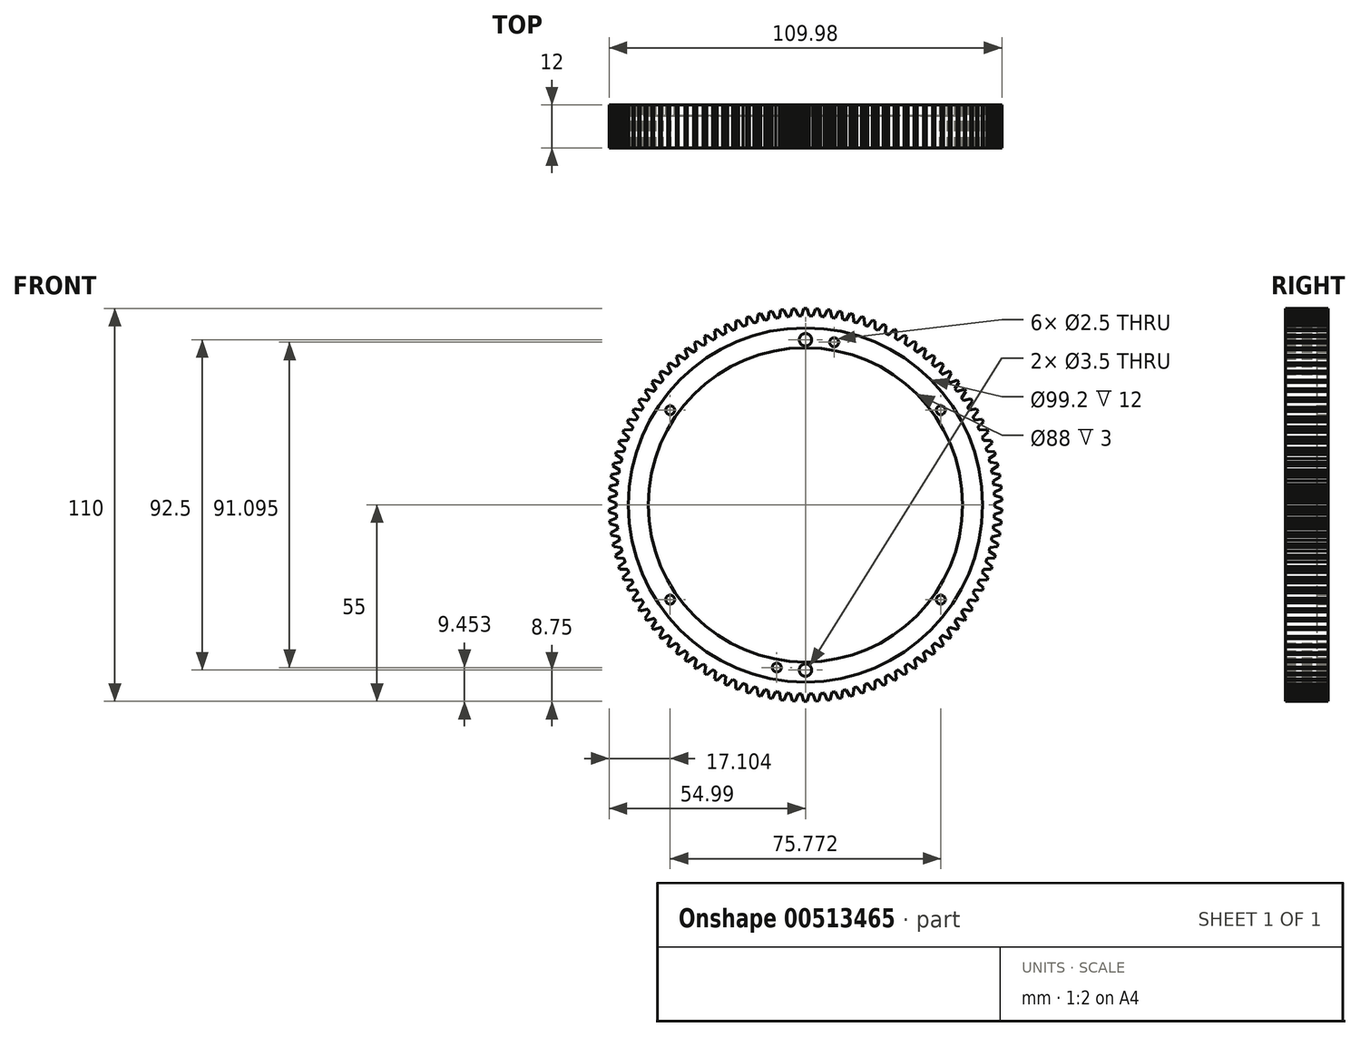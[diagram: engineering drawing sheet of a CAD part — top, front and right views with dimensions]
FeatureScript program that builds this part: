
annotation { "Feature Type Name" : "Feature", "Feature Type Description" : "" }
export const myFeature = defineFeature(function(context is Context, id is Id, definition is map)
    precondition{}
    {
        {
            var Q0;
            Q0=qCreatedBy(makeId("Front.planeOp"),FACE);
            var sketch = newSketch(context, id + "F0", { "sketchPlane" : qUnion([Q0])});
            skLineSegment(sketch, "E0", {"start": v(0, 0) * mm, "end": v(0, 53) * mm, "construction": true});
            skLineSegment(sketch, "E1", {"start": v(0, 55) * mm, "end": v(-0.4, 55) * mm});
            skLineSegment(sketch, "E2.MirrorCS", {"start": v(0, 55) * mm, "end": v(0.4, 55) * mm});
            skPoint(sketch, "E3.center", {"position": v(0, 0) * mm});
            skCircle(sketch, "E4", {"center": v(0, 0) * mm, "radius": 44 * mm});
            skCircle(sketch, "E5", {"center": v(0, 0) * mm, "radius": 46.25 * mm});
            skCircle(sketch, "E6", {"center": v(0, 0) * mm, "radius": 49.4 * mm});
            skCircle(sketch, "E7", {"center": v(0, 0) * mm, "radius": 49.6 * mm});
            skLineSegment(sketch, "E8", {"start": v(0, 0) * mm, "end": v(12.55, 71.2) * mm, "construction": true});
            skLineSegment(sketch, "E9", {"start": v(0, 0) * mm, "end": v(68.64, 48.06) * mm, "construction": true});
            skLineSegment(sketch, "E10", {"start": v(0, 0) * mm, "end": v(80.2, -56.16) * mm, "construction": true});
            skCircle(sketch, "E11", {"center": v(8.03, 45.55) * mm, "radius": 1.1 * mm});
            skCircle(sketch, "E12", {"center": v(37.89, 26.53) * mm, "radius": 1.1 * mm});
            skCircle(sketch, "E13", {"center": v(37.89, -26.53) * mm, "radius": 1.1 * mm});
            skLineSegment(sketch, "E14", {"start": v(0, 0) * mm, "end": v(0, -53) * mm, "construction": true});
            skLineSegment(sketch, "E15.MirrorCS", {"start": v(0, 0) * mm, "end": v(-80.2, -56.16) * mm, "construction": true});
            skCircle(sketch, "E16.MirrorC", {"center": v(-37.89, -26.53) * mm, "radius": 1.1 * mm});
            skLineSegment(sketch, "E17", {"start": v(0, 0) * mm, "end": v(-12.24, -69.4) * mm, "construction": true});
            skCircle(sketch, "E18", {"center": v(-8.03, -45.55) * mm, "radius": 1.1 * mm});
            skLineSegment(sketch, "E19.MirrorCS", {"start": v(0, 0) * mm, "end": v(-68.64, 48.06) * mm, "construction": true});
            skCircle(sketch, "E20.MirrorC", {"center": v(-37.89, 26.53) * mm, "radius": 1.1 * mm});
            skCircle(sketch, "E21", {"center": v(0, -46.25) * mm, "radius": 1.75 * mm});
            skCircle(sketch, "E22", {"center": v(0, 46.25) * mm, "radius": 1.75 * mm});
            skLineSegment(sketch, "E23", {"start": v(-0.4, 55) * mm, "end": v(-1.09, 52.99) * mm});
            skLineSegment(sketch, "E24", {"start": v(0.4, 55) * mm, "end": v(1.09, 52.99) * mm});
            skCircle(sketch, "E25", {"center": v(0, 0) * mm, "radius": 53 * mm});
            skLineSegment(sketch, "E26.1.0", {"start": v(-3.66, 54.88) * mm, "end": v(-4.23, 52.83) * mm});
            skLineSegment(sketch, "E26.1.1", {"start": v(-3.26, 54.9) * mm, "end": v(-3.66, 54.88) * mm});
            skLineSegment(sketch, "E26.1.2", {"start": v(-3.26, 54.9) * mm, "end": v(-2.85, 54.93) * mm});
            skLineSegment(sketch, "E26.1.3", {"start": v(-2.85, 54.93) * mm, "end": v(-2.05, 52.96) * mm});
            skLineSegment(sketch, "E26.2.0", {"start": v(-6.9, 54.57) * mm, "end": v(-7.35, 52.49) * mm});
            skLineSegment(sketch, "E26.2.1", {"start": v(-6.5, 54.61) * mm, "end": v(-6.9, 54.57) * mm});
            skLineSegment(sketch, "E26.2.2", {"start": v(-6.5, 54.61) * mm, "end": v(-6.1, 54.66) * mm});
            skLineSegment(sketch, "E26.2.3", {"start": v(-6.1, 54.66) * mm, "end": v(-5.19, 52.75) * mm});
            skLineSegment(sketch, "E26.3.0", {"start": v(-10.13, 54.06) * mm, "end": v(-10.45, 51.96) * mm});
            skLineSegment(sketch, "E26.3.1", {"start": v(-9.73, 54.13) * mm, "end": v(-10.13, 54.06) * mm});
            skLineSegment(sketch, "E26.3.2", {"start": v(-9.73, 54.13) * mm, "end": v(-9.33, 54.2) * mm});
            skLineSegment(sketch, "E26.3.3", {"start": v(-9.33, 54.2) * mm, "end": v(-8.3, 52.35) * mm});
            skLineSegment(sketch, "E26.4.0", {"start": v(-13.31, 53.37) * mm, "end": v(-13.5, 51.25) * mm});
            skLineSegment(sketch, "E26.4.1", {"start": v(-12.92, 53.46) * mm, "end": v(-13.31, 53.37) * mm});
            skLineSegment(sketch, "E26.4.2", {"start": v(-12.92, 53.46) * mm, "end": v(-12.53, 53.56) * mm});
            skLineSegment(sketch, "E26.4.3", {"start": v(-12.53, 53.56) * mm, "end": v(-11.39, 51.76) * mm});
            skLineSegment(sketch, "E26.5.0", {"start": v(-16.45, 52.48) * mm, "end": v(-16.52, 50.36) * mm});
            skLineSegment(sketch, "E26.5.1", {"start": v(-16.06, 52.6) * mm, "end": v(-16.45, 52.48) * mm});
            skLineSegment(sketch, "E26.5.2", {"start": v(-16.06, 52.6) * mm, "end": v(-15.68, 52.72) * mm});
            skLineSegment(sketch, "E26.5.3", {"start": v(-15.68, 52.72) * mm, "end": v(-14.43, 51) * mm});
            skLineSegment(sketch, "E26.6.0", {"start": v(-19.53, 51.42) * mm, "end": v(-19.47, 49.3) * mm});
            skLineSegment(sketch, "E26.6.1", {"start": v(-19.15, 51.56) * mm, "end": v(-19.53, 51.42) * mm});
            skLineSegment(sketch, "E26.6.2", {"start": v(-19.15, 51.56) * mm, "end": v(-18.77, 51.7) * mm});
            skLineSegment(sketch, "E26.6.3", {"start": v(-18.77, 51.7) * mm, "end": v(-17.43, 50.05) * mm});
            skLineSegment(sketch, "E26.7.0", {"start": v(-22.54, 50.17) * mm, "end": v(-22.36, 48.05) * mm});
            skLineSegment(sketch, "E26.7.1", {"start": v(-22.17, 50.33) * mm, "end": v(-22.54, 50.17) * mm});
            skLineSegment(sketch, "E26.7.2", {"start": v(-22.17, 50.33) * mm, "end": v(-21.8, 50.5) * mm});
            skLineSegment(sketch, "E26.7.3", {"start": v(-21.8, 50.5) * mm, "end": v(-20.36, 48.93) * mm});
            skLineSegment(sketch, "E26.8.0", {"start": v(-25.47, 48.75) * mm, "end": v(-25.17, 46.64) * mm});
            skLineSegment(sketch, "E26.8.1", {"start": v(-25.11, 48.93) * mm, "end": v(-25.47, 48.75) * mm});
            skLineSegment(sketch, "E26.8.2", {"start": v(-25.11, 48.93) * mm, "end": v(-24.75, 49.12) * mm});
            skLineSegment(sketch, "E26.8.3", {"start": v(-24.75, 49.12) * mm, "end": v(-23.23, 47.64) * mm});
            skLineSegment(sketch, "E26.9.0", {"start": v(-28.32, 47.15) * mm, "end": v(-27.88, 45.07) * mm});
            skLineSegment(sketch, "E26.9.1", {"start": v(-27.97, 47.36) * mm, "end": v(-28.32, 47.15) * mm});
            skLineSegment(sketch, "E26.9.2", {"start": v(-27.97, 47.36) * mm, "end": v(-27.62, 47.56) * mm});
            skLineSegment(sketch, "E26.9.3", {"start": v(-27.62, 47.56) * mm, "end": v(-26, 46.18) * mm});
            skLineSegment(sketch, "E26.10.0", {"start": v(-31.06, 45.4) * mm, "end": v(-30.5, 43.34) * mm});
            skLineSegment(sketch, "E26.10.1", {"start": v(-30.73, 45.62) * mm, "end": v(-31.06, 45.4) * mm});
            skLineSegment(sketch, "E26.10.2", {"start": v(-30.73, 45.62) * mm, "end": v(-30.39, 45.84) * mm});
            skLineSegment(sketch, "E26.10.3", {"start": v(-30.39, 45.84) * mm, "end": v(-28.7, 44.56) * mm});
            skLineSegment(sketch, "E26.11.0", {"start": v(-33.7, 43.47) * mm, "end": v(-33.02, 41.46) * mm});
            skLineSegment(sketch, "E26.11.1", {"start": v(-33.37, 43.72) * mm, "end": v(-33.7, 43.47) * mm});
            skLineSegment(sketch, "E26.11.2", {"start": v(-33.37, 43.72) * mm, "end": v(-33.05, 43.96) * mm});
            skLineSegment(sketch, "E26.11.3", {"start": v(-33.05, 43.96) * mm, "end": v(-31.29, 42.78) * mm});
            skLineSegment(sketch, "E26.12.0", {"start": v(-36.21, 41.4) * mm, "end": v(-35.42, 39.43) * mm});
            skLineSegment(sketch, "E26.12.1", {"start": v(-35.9, 41.66) * mm, "end": v(-36.21, 41.4) * mm});
            skLineSegment(sketch, "E26.12.2", {"start": v(-35.9, 41.66) * mm, "end": v(-35.6, 41.93) * mm});
            skLineSegment(sketch, "E26.12.3", {"start": v(-35.6, 41.93) * mm, "end": v(-33.77, 40.85) * mm});
            skLineSegment(sketch, "E26.13.0", {"start": v(-38.6, 39.18) * mm, "end": v(-37.7, 37.26) * mm});
            skLineSegment(sketch, "E26.13.1", {"start": v(-38.31, 39.46) * mm, "end": v(-38.6, 39.18) * mm});
            skLineSegment(sketch, "E26.13.2", {"start": v(-38.31, 39.46) * mm, "end": v(-38.02, 39.75) * mm});
            skLineSegment(sketch, "E26.13.3", {"start": v(-38.02, 39.75) * mm, "end": v(-36.13, 38.78) * mm});
            skLineSegment(sketch, "E26.14.0", {"start": v(-40.85, 36.83) * mm, "end": v(-39.83, 34.96) * mm});
            skLineSegment(sketch, "E26.14.1", {"start": v(-40.58, 37.12) * mm, "end": v(-40.85, 36.83) * mm});
            skLineSegment(sketch, "E26.14.2", {"start": v(-40.58, 37.12) * mm, "end": v(-40.3, 37.42) * mm});
            skLineSegment(sketch, "E26.14.3", {"start": v(-40.3, 37.42) * mm, "end": v(-38.36, 36.57) * mm});
            skLineSegment(sketch, "E26.15.0", {"start": v(-42.96, 34.34) * mm, "end": v(-41.83, 32.54) * mm});
            skLineSegment(sketch, "E26.15.1", {"start": v(-42.7, 34.65) * mm, "end": v(-42.96, 34.34) * mm});
            skLineSegment(sketch, "E26.15.2", {"start": v(-42.7, 34.65) * mm, "end": v(-42.45, 34.97) * mm});
            skLineSegment(sketch, "E26.15.3", {"start": v(-42.45, 34.97) * mm, "end": v(-40.46, 34.23) * mm});
            skLineSegment(sketch, "E27.2.16.0", {"start": v(-44.92, 31.73) * mm, "end": v(-43.69, 30) * mm});
            skLineSegment(sketch, "E27.3.16.0", {"start": v(-44.69, 32.06) * mm, "end": v(-44.92, 31.73) * mm});
            skLineSegment(sketch, "E27.6.16.0", {"start": v(-44.69, 32.06) * mm, "end": v(-44.45, 32.4) * mm});
            skLineSegment(sketch, "E27.9.16.0", {"start": v(-44.45, 32.4) * mm, "end": v(-42.42, 31.78) * mm});
            skLineSegment(sketch, "E27.2.17.0", {"start": v(-46.72, 29.02) * mm, "end": v(-45.39, 27.37) * mm});
            skLineSegment(sketch, "E27.3.17.0", {"start": v(-46.5, 29.36) * mm, "end": v(-46.72, 29.02) * mm});
            skLineSegment(sketch, "E27.6.17.0", {"start": v(-46.5, 29.36) * mm, "end": v(-46.3, 29.7) * mm});
            skLineSegment(sketch, "E27.9.17.0", {"start": v(-46.3, 29.7) * mm, "end": v(-44.23, 29.2) * mm});
            skLineSegment(sketch, "E27.2.18.0", {"start": v(-48.36, 26.2) * mm, "end": v(-46.93, 24.63) * mm});
            skLineSegment(sketch, "E27.3.18.0", {"start": v(-48.17, 26.55) * mm, "end": v(-48.36, 26.2) * mm});
            skLineSegment(sketch, "E27.6.18.0", {"start": v(-48.17, 26.55) * mm, "end": v(-47.97, 26.9) * mm});
            skLineSegment(sketch, "E27.9.18.0", {"start": v(-47.97, 26.9) * mm, "end": v(-45.88, 26.54) * mm});
            skLineSegment(sketch, "E27.2.19.0", {"start": v(-49.83, 23.29) * mm, "end": v(-48.3, 21.8) * mm});
            skLineSegment(sketch, "E27.3.19.0", {"start": v(-49.65, 23.65) * mm, "end": v(-49.83, 23.29) * mm});
            skLineSegment(sketch, "E27.6.19.0", {"start": v(-49.65, 23.65) * mm, "end": v(-49.48, 24.02) * mm});
            skLineSegment(sketch, "E27.9.19.0", {"start": v(-49.48, 24.02) * mm, "end": v(-47.37, 23.77) * mm});
            skLineSegment(sketch, "E27.2.20.0", {"start": v(-51.12, 20.3) * mm, "end": v(-49.51, 18.9) * mm});
            skLineSegment(sketch, "E27.3.20.0", {"start": v(-50.97, 20.67) * mm, "end": v(-51.12, 20.3) * mm});
            skLineSegment(sketch, "E27.6.20.0", {"start": v(-50.97, 20.67) * mm, "end": v(-50.82, 21.05) * mm});
            skLineSegment(sketch, "E27.9.20.0", {"start": v(-50.82, 21.05) * mm, "end": v(-48.7, 20.92) * mm});
            skLineSegment(sketch, "E27.2.21.0", {"start": v(-52.23, 17.23) * mm, "end": v(-50.55, 15.94) * mm});
            skLineSegment(sketch, "E27.3.21.0", {"start": v(-52.1, 17.61) * mm, "end": v(-52.23, 17.23) * mm});
            skLineSegment(sketch, "E27.6.21.0", {"start": v(-52.1, 17.61) * mm, "end": v(-51.97, 18) * mm});
            skLineSegment(sketch, "E27.9.21.0", {"start": v(-51.97, 18) * mm, "end": v(-49.85, 18) * mm});
            skLineSegment(sketch, "E27.2.22.0", {"start": v(-53.16, 14.1) * mm, "end": v(-51.4, 12.92) * mm});
            skLineSegment(sketch, "E27.3.22.0", {"start": v(-53.05, 14.5) * mm, "end": v(-53.16, 14.1) * mm});
            skLineSegment(sketch, "E27.6.22.0", {"start": v(-53.05, 14.5) * mm, "end": v(-52.95, 14.89) * mm});
            skLineSegment(sketch, "E27.9.22.0", {"start": v(-52.95, 14.89) * mm, "end": v(-50.83, 15.02) * mm});
            skLineSegment(sketch, "E27.2.23.0", {"start": v(-53.9, 10.93) * mm, "end": v(-52.08, 9.85) * mm});
            skLineSegment(sketch, "E27.3.23.0", {"start": v(-53.82, 11.33) * mm, "end": v(-53.9, 10.93) * mm});
            skLineSegment(sketch, "E27.6.23.0", {"start": v(-53.82, 11.33) * mm, "end": v(-53.74, 11.73) * mm});
            skLineSegment(sketch, "E27.9.23.0", {"start": v(-53.74, 11.73) * mm, "end": v(-51.63, 11.98) * mm});
            skLineSegment(sketch, "E27.2.24.0", {"start": v(-54.46, 7.72) * mm, "end": v(-52.57, 6.75) * mm});
            skLineSegment(sketch, "E27.3.24.0", {"start": v(-54.4, 8.12) * mm, "end": v(-54.46, 7.72) * mm});
            skLineSegment(sketch, "E27.6.24.0", {"start": v(-54.4, 8.12) * mm, "end": v(-54.34, 8.52) * mm});
            skLineSegment(sketch, "E27.9.24.0", {"start": v(-54.34, 8.52) * mm, "end": v(-52.25, 8.9) * mm});
            skLineSegment(sketch, "E27.2.25.0", {"start": v(-54.82, 4.48) * mm, "end": v(-52.88, 3.62) * mm});
            skLineSegment(sketch, "E27.3.25.0", {"start": v(-54.78, 4.88) * mm, "end": v(-54.82, 4.48) * mm});
            skLineSegment(sketch, "E27.6.25.0", {"start": v(-54.78, 4.88) * mm, "end": v(-54.75, 5.29) * mm});
            skLineSegment(sketch, "E27.9.25.0", {"start": v(-54.75, 5.29) * mm, "end": v(-52.68, 5.8) * mm});
            skLineSegment(sketch, "E27.2.26.0", {"start": v(-54.99, 1.23) * mm, "end": v(-53, 0.48) * mm});
            skLineSegment(sketch, "E27.3.26.0", {"start": v(-54.98, 1.63) * mm, "end": v(-54.99, 1.23) * mm});
            skLineSegment(sketch, "E27.6.26.0", {"start": v(-54.98, 1.63) * mm, "end": v(-54.96, 2.03) * mm});
            skLineSegment(sketch, "E27.9.26.0", {"start": v(-54.96, 2.03) * mm, "end": v(-52.93, 2.66) * mm});
            skLineSegment(sketch, "E27.2.27.0", {"start": v(-54.96, -2.03) * mm, "end": v(-52.93, -2.66) * mm});
            skLineSegment(sketch, "E27.3.27.0", {"start": v(-54.98, -1.63) * mm, "end": v(-54.96, -2.03) * mm});
            skLineSegment(sketch, "E27.6.27.0", {"start": v(-54.98, -1.63) * mm, "end": v(-54.99, -1.23) * mm});
            skLineSegment(sketch, "E27.9.27.0", {"start": v(-54.99, -1.23) * mm, "end": v(-53, -0.48) * mm});
            skLineSegment(sketch, "E27.2.28.0", {"start": v(-54.75, -5.29) * mm, "end": v(-52.68, -5.8) * mm});
            skLineSegment(sketch, "E27.3.28.0", {"start": v(-54.78, -4.88) * mm, "end": v(-54.75, -5.29) * mm});
            skLineSegment(sketch, "E27.6.28.0", {"start": v(-54.78, -4.88) * mm, "end": v(-54.82, -4.48) * mm});
            skLineSegment(sketch, "E27.9.28.0", {"start": v(-54.82, -4.48) * mm, "end": v(-52.88, -3.62) * mm});
            skLineSegment(sketch, "E27.2.29.0", {"start": v(-54.34, -8.52) * mm, "end": v(-52.25, -8.9) * mm});
            skLineSegment(sketch, "E27.3.29.0", {"start": v(-54.4, -8.12) * mm, "end": v(-54.34, -8.52) * mm});
            skLineSegment(sketch, "E27.6.29.0", {"start": v(-54.4, -8.12) * mm, "end": v(-54.46, -7.72) * mm});
            skLineSegment(sketch, "E27.9.29.0", {"start": v(-54.46, -7.72) * mm, "end": v(-52.57, -6.75) * mm});
            skLineSegment(sketch, "E27.2.30.0", {"start": v(-53.74, -11.73) * mm, "end": v(-51.63, -11.98) * mm});
            skLineSegment(sketch, "E27.3.30.0", {"start": v(-53.82, -11.33) * mm, "end": v(-53.74, -11.73) * mm});
            skLineSegment(sketch, "E27.6.30.0", {"start": v(-53.82, -11.33) * mm, "end": v(-53.9, -10.93) * mm});
            skLineSegment(sketch, "E27.9.30.0", {"start": v(-53.9, -10.93) * mm, "end": v(-52.08, -9.85) * mm});
            skLineSegment(sketch, "E27.2.31.0", {"start": v(-52.95, -14.89) * mm, "end": v(-50.83, -15.02) * mm});
            skLineSegment(sketch, "E27.3.31.0", {"start": v(-53.05, -14.5) * mm, "end": v(-52.95, -14.89) * mm});
            skLineSegment(sketch, "E27.6.31.0", {"start": v(-53.05, -14.5) * mm, "end": v(-53.16, -14.1) * mm});
            skLineSegment(sketch, "E27.9.31.0", {"start": v(-53.16, -14.1) * mm, "end": v(-51.4, -12.92) * mm});
            skLineSegment(sketch, "E27.2.32.0", {"start": v(-51.97, -18) * mm, "end": v(-49.85, -18) * mm});
            skLineSegment(sketch, "E27.3.32.0", {"start": v(-52.1, -17.61) * mm, "end": v(-51.97, -18) * mm});
            skLineSegment(sketch, "E27.6.32.0", {"start": v(-52.1, -17.61) * mm, "end": v(-52.23, -17.23) * mm});
            skLineSegment(sketch, "E27.9.32.0", {"start": v(-52.23, -17.23) * mm, "end": v(-50.55, -15.94) * mm});
            skLineSegment(sketch, "E27.2.33.0", {"start": v(-50.82, -21.05) * mm, "end": v(-48.7, -20.92) * mm});
            skLineSegment(sketch, "E27.3.33.0", {"start": v(-50.97, -20.67) * mm, "end": v(-50.82, -21.05) * mm});
            skLineSegment(sketch, "E27.6.33.0", {"start": v(-50.97, -20.67) * mm, "end": v(-51.12, -20.3) * mm});
            skLineSegment(sketch, "E27.9.33.0", {"start": v(-51.12, -20.3) * mm, "end": v(-49.51, -18.9) * mm});
            skLineSegment(sketch, "E27.2.34.0", {"start": v(-49.48, -24.02) * mm, "end": v(-47.37, -23.77) * mm});
            skLineSegment(sketch, "E27.3.34.0", {"start": v(-49.65, -23.65) * mm, "end": v(-49.48, -24.02) * mm});
            skLineSegment(sketch, "E27.6.34.0", {"start": v(-49.65, -23.65) * mm, "end": v(-49.83, -23.29) * mm});
            skLineSegment(sketch, "E27.9.34.0", {"start": v(-49.83, -23.29) * mm, "end": v(-48.3, -21.8) * mm});
            skLineSegment(sketch, "E27.2.35.0", {"start": v(-47.97, -26.9) * mm, "end": v(-45.88, -26.54) * mm});
            skLineSegment(sketch, "E27.3.35.0", {"start": v(-48.17, -26.55) * mm, "end": v(-47.97, -26.9) * mm});
            skLineSegment(sketch, "E27.6.35.0", {"start": v(-48.17, -26.55) * mm, "end": v(-48.36, -26.2) * mm});
            skLineSegment(sketch, "E27.9.35.0", {"start": v(-48.36, -26.2) * mm, "end": v(-46.93, -24.63) * mm});
            skLineSegment(sketch, "E27.2.36.0", {"start": v(-46.3, -29.7) * mm, "end": v(-44.23, -29.2) * mm});
            skLineSegment(sketch, "E27.3.36.0", {"start": v(-46.5, -29.36) * mm, "end": v(-46.3, -29.7) * mm});
            skLineSegment(sketch, "E27.6.36.0", {"start": v(-46.5, -29.36) * mm, "end": v(-46.72, -29.02) * mm});
            skLineSegment(sketch, "E27.9.36.0", {"start": v(-46.72, -29.02) * mm, "end": v(-45.39, -27.37) * mm});
            skLineSegment(sketch, "E27.2.37.0", {"start": v(-44.45, -32.4) * mm, "end": v(-42.42, -31.78) * mm});
            skLineSegment(sketch, "E27.3.37.0", {"start": v(-44.69, -32.06) * mm, "end": v(-44.45, -32.4) * mm});
            skLineSegment(sketch, "E27.6.37.0", {"start": v(-44.69, -32.06) * mm, "end": v(-44.92, -31.73) * mm});
            skLineSegment(sketch, "E27.9.37.0", {"start": v(-44.92, -31.73) * mm, "end": v(-43.69, -30) * mm});
            skLineSegment(sketch, "E27.2.38.0", {"start": v(-42.45, -34.97) * mm, "end": v(-40.46, -34.23) * mm});
            skLineSegment(sketch, "E27.3.38.0", {"start": v(-42.7, -34.65) * mm, "end": v(-42.45, -34.97) * mm});
            skLineSegment(sketch, "E27.6.38.0", {"start": v(-42.7, -34.65) * mm, "end": v(-42.96, -34.34) * mm});
            skLineSegment(sketch, "E27.9.38.0", {"start": v(-42.96, -34.34) * mm, "end": v(-41.83, -32.54) * mm});
            skLineSegment(sketch, "E27.2.39.0", {"start": v(-40.3, -37.42) * mm, "end": v(-38.36, -36.57) * mm});
            skLineSegment(sketch, "E27.3.39.0", {"start": v(-40.58, -37.12) * mm, "end": v(-40.3, -37.42) * mm});
            skLineSegment(sketch, "E27.6.39.0", {"start": v(-40.58, -37.12) * mm, "end": v(-40.85, -36.83) * mm});
            skLineSegment(sketch, "E27.9.39.0", {"start": v(-40.85, -36.83) * mm, "end": v(-39.83, -34.96) * mm});
            skLineSegment(sketch, "E27.2.40.0", {"start": v(-38.02, -39.75) * mm, "end": v(-36.13, -38.78) * mm});
            skLineSegment(sketch, "E27.3.40.0", {"start": v(-38.31, -39.46) * mm, "end": v(-38.02, -39.75) * mm});
            skLineSegment(sketch, "E27.6.40.0", {"start": v(-38.31, -39.46) * mm, "end": v(-38.6, -39.18) * mm});
            skLineSegment(sketch, "E27.9.40.0", {"start": v(-38.6, -39.18) * mm, "end": v(-37.7, -37.26) * mm});
            skLineSegment(sketch, "E27.2.41.0", {"start": v(-35.6, -41.93) * mm, "end": v(-33.77, -40.85) * mm});
            skLineSegment(sketch, "E27.3.41.0", {"start": v(-35.9, -41.66) * mm, "end": v(-35.6, -41.93) * mm});
            skLineSegment(sketch, "E27.6.41.0", {"start": v(-35.9, -41.66) * mm, "end": v(-36.21, -41.4) * mm});
            skLineSegment(sketch, "E27.9.41.0", {"start": v(-36.21, -41.4) * mm, "end": v(-35.42, -39.43) * mm});
            skLineSegment(sketch, "E27.2.42.0", {"start": v(-33.05, -43.96) * mm, "end": v(-31.29, -42.78) * mm});
            skLineSegment(sketch, "E27.3.42.0", {"start": v(-33.37, -43.72) * mm, "end": v(-33.05, -43.96) * mm});
            skLineSegment(sketch, "E27.6.42.0", {"start": v(-33.37, -43.72) * mm, "end": v(-33.7, -43.47) * mm});
            skLineSegment(sketch, "E27.9.42.0", {"start": v(-33.7, -43.47) * mm, "end": v(-33.02, -41.46) * mm});
            skLineSegment(sketch, "E27.2.43.0", {"start": v(-30.39, -45.84) * mm, "end": v(-28.7, -44.56) * mm});
            skLineSegment(sketch, "E27.3.43.0", {"start": v(-30.73, -45.62) * mm, "end": v(-30.39, -45.84) * mm});
            skLineSegment(sketch, "E27.6.43.0", {"start": v(-30.73, -45.62) * mm, "end": v(-31.06, -45.4) * mm});
            skLineSegment(sketch, "E27.9.43.0", {"start": v(-31.06, -45.4) * mm, "end": v(-30.5, -43.34) * mm});
            skLineSegment(sketch, "E27.2.44.0", {"start": v(-27.62, -47.56) * mm, "end": v(-26, -46.18) * mm});
            skLineSegment(sketch, "E27.3.44.0", {"start": v(-27.97, -47.36) * mm, "end": v(-27.62, -47.56) * mm});
            skLineSegment(sketch, "E27.6.44.0", {"start": v(-27.97, -47.36) * mm, "end": v(-28.32, -47.15) * mm});
            skLineSegment(sketch, "E27.9.44.0", {"start": v(-28.32, -47.15) * mm, "end": v(-27.88, -45.07) * mm});
            skLineSegment(sketch, "E27.2.45.0", {"start": v(-24.75, -49.12) * mm, "end": v(-23.23, -47.64) * mm});
            skLineSegment(sketch, "E27.3.45.0", {"start": v(-25.11, -48.93) * mm, "end": v(-24.75, -49.12) * mm});
            skLineSegment(sketch, "E27.6.45.0", {"start": v(-25.11, -48.93) * mm, "end": v(-25.47, -48.75) * mm});
            skLineSegment(sketch, "E27.9.45.0", {"start": v(-25.47, -48.75) * mm, "end": v(-25.17, -46.64) * mm});
            skLineSegment(sketch, "E27.2.46.0", {"start": v(-21.8, -50.5) * mm, "end": v(-20.36, -48.93) * mm});
            skLineSegment(sketch, "E27.3.46.0", {"start": v(-22.17, -50.33) * mm, "end": v(-21.8, -50.5) * mm});
            skLineSegment(sketch, "E27.6.46.0", {"start": v(-22.17, -50.33) * mm, "end": v(-22.54, -50.17) * mm});
            skLineSegment(sketch, "E27.9.46.0", {"start": v(-22.54, -50.17) * mm, "end": v(-22.36, -48.05) * mm});
            skLineSegment(sketch, "E27.2.47.0", {"start": v(-18.77, -51.7) * mm, "end": v(-17.43, -50.05) * mm});
            skLineSegment(sketch, "E27.3.47.0", {"start": v(-19.15, -51.56) * mm, "end": v(-18.77, -51.7) * mm});
            skLineSegment(sketch, "E27.6.47.0", {"start": v(-19.15, -51.56) * mm, "end": v(-19.53, -51.42) * mm});
            skLineSegment(sketch, "E27.9.47.0", {"start": v(-19.53, -51.42) * mm, "end": v(-19.47, -49.3) * mm});
            skLineSegment(sketch, "E27.2.48.0", {"start": v(-15.68, -52.72) * mm, "end": v(-14.43, -51) * mm});
            skLineSegment(sketch, "E27.3.48.0", {"start": v(-16.06, -52.6) * mm, "end": v(-15.68, -52.72) * mm});
            skLineSegment(sketch, "E27.6.48.0", {"start": v(-16.06, -52.6) * mm, "end": v(-16.45, -52.48) * mm});
            skLineSegment(sketch, "E27.9.48.0", {"start": v(-16.45, -52.48) * mm, "end": v(-16.52, -50.36) * mm});
            skLineSegment(sketch, "E27.2.49.0", {"start": v(-12.53, -53.56) * mm, "end": v(-11.39, -51.76) * mm});
            skLineSegment(sketch, "E27.3.49.0", {"start": v(-12.92, -53.46) * mm, "end": v(-12.53, -53.56) * mm});
            skLineSegment(sketch, "E27.6.49.0", {"start": v(-12.92, -53.46) * mm, "end": v(-13.31, -53.37) * mm});
            skLineSegment(sketch, "E27.9.49.0", {"start": v(-13.31, -53.37) * mm, "end": v(-13.5, -51.25) * mm});
            skLineSegment(sketch, "E27.2.50.0", {"start": v(-9.33, -54.2) * mm, "end": v(-8.3, -52.35) * mm});
            skLineSegment(sketch, "E27.3.50.0", {"start": v(-9.73, -54.13) * mm, "end": v(-9.33, -54.2) * mm});
            skLineSegment(sketch, "E27.6.50.0", {"start": v(-9.73, -54.13) * mm, "end": v(-10.13, -54.06) * mm});
            skLineSegment(sketch, "E27.9.50.0", {"start": v(-10.13, -54.06) * mm, "end": v(-10.45, -51.96) * mm});
            skLineSegment(sketch, "E27.2.51.0", {"start": v(-6.1, -54.66) * mm, "end": v(-5.19, -52.75) * mm});
            skLineSegment(sketch, "E27.3.51.0", {"start": v(-6.5, -54.61) * mm, "end": v(-6.1, -54.66) * mm});
            skLineSegment(sketch, "E27.6.51.0", {"start": v(-6.5, -54.61) * mm, "end": v(-6.9, -54.57) * mm});
            skLineSegment(sketch, "E27.9.51.0", {"start": v(-6.9, -54.57) * mm, "end": v(-7.35, -52.49) * mm});
            skLineSegment(sketch, "E27.2.52.0", {"start": v(-2.85, -54.93) * mm, "end": v(-2.05, -52.96) * mm});
            skLineSegment(sketch, "E27.3.52.0", {"start": v(-3.26, -54.9) * mm, "end": v(-2.85, -54.93) * mm});
            skLineSegment(sketch, "E27.6.52.0", {"start": v(-3.26, -54.9) * mm, "end": v(-3.66, -54.88) * mm});
            skLineSegment(sketch, "E27.9.52.0", {"start": v(-3.66, -54.88) * mm, "end": v(-4.23, -52.83) * mm});
            skLineSegment(sketch, "E27.2.53.0", {"start": v(0.4, -55) * mm, "end": v(1.09, -52.99) * mm});
            skLineSegment(sketch, "E27.3.53.0", {"start": v(0, -55) * mm, "end": v(0.4, -55) * mm});
            skLineSegment(sketch, "E27.6.53.0", {"start": v(0, -55) * mm, "end": v(-0.4, -55) * mm});
            skLineSegment(sketch, "E27.9.53.0", {"start": v(-0.4, -55) * mm, "end": v(-1.09, -52.99) * mm});
            skLineSegment(sketch, "E27.2.54.0", {"start": v(3.66, -54.88) * mm, "end": v(4.23, -52.83) * mm});
            skLineSegment(sketch, "E27.3.54.0", {"start": v(3.26, -54.9) * mm, "end": v(3.66, -54.88) * mm});
            skLineSegment(sketch, "E27.6.54.0", {"start": v(3.26, -54.9) * mm, "end": v(2.85, -54.93) * mm});
            skLineSegment(sketch, "E27.9.54.0", {"start": v(2.85, -54.93) * mm, "end": v(2.05, -52.96) * mm});
            skLineSegment(sketch, "E27.2.55.0", {"start": v(6.9, -54.57) * mm, "end": v(7.35, -52.49) * mm});
            skLineSegment(sketch, "E27.3.55.0", {"start": v(6.5, -54.61) * mm, "end": v(6.9, -54.57) * mm});
            skLineSegment(sketch, "E27.6.55.0", {"start": v(6.5, -54.61) * mm, "end": v(6.1, -54.66) * mm});
            skLineSegment(sketch, "E27.9.55.0", {"start": v(6.1, -54.66) * mm, "end": v(5.19, -52.75) * mm});
            skLineSegment(sketch, "E27.2.56.0", {"start": v(10.13, -54.06) * mm, "end": v(10.45, -51.96) * mm});
            skLineSegment(sketch, "E27.3.56.0", {"start": v(9.73, -54.13) * mm, "end": v(10.13, -54.06) * mm});
            skLineSegment(sketch, "E27.6.56.0", {"start": v(9.73, -54.13) * mm, "end": v(9.33, -54.2) * mm});
            skLineSegment(sketch, "E27.9.56.0", {"start": v(9.33, -54.2) * mm, "end": v(8.3, -52.35) * mm});
            skLineSegment(sketch, "E27.2.57.0", {"start": v(13.31, -53.37) * mm, "end": v(13.5, -51.25) * mm});
            skLineSegment(sketch, "E27.3.57.0", {"start": v(12.92, -53.46) * mm, "end": v(13.31, -53.37) * mm});
            skLineSegment(sketch, "E27.6.57.0", {"start": v(12.92, -53.46) * mm, "end": v(12.53, -53.56) * mm});
            skLineSegment(sketch, "E27.9.57.0", {"start": v(12.53, -53.56) * mm, "end": v(11.39, -51.76) * mm});
            skLineSegment(sketch, "E27.2.58.0", {"start": v(16.45, -52.48) * mm, "end": v(16.52, -50.36) * mm});
            skLineSegment(sketch, "E27.3.58.0", {"start": v(16.06, -52.6) * mm, "end": v(16.45, -52.48) * mm});
            skLineSegment(sketch, "E27.6.58.0", {"start": v(16.06, -52.6) * mm, "end": v(15.68, -52.72) * mm});
            skLineSegment(sketch, "E27.9.58.0", {"start": v(15.68, -52.72) * mm, "end": v(14.43, -51) * mm});
            skLineSegment(sketch, "E27.2.59.0", {"start": v(19.53, -51.42) * mm, "end": v(19.47, -49.3) * mm});
            skLineSegment(sketch, "E27.3.59.0", {"start": v(19.15, -51.56) * mm, "end": v(19.53, -51.42) * mm});
            skLineSegment(sketch, "E27.6.59.0", {"start": v(19.15, -51.56) * mm, "end": v(18.77, -51.7) * mm});
            skLineSegment(sketch, "E27.9.59.0", {"start": v(18.77, -51.7) * mm, "end": v(17.43, -50.05) * mm});
            skLineSegment(sketch, "E27.2.60.0", {"start": v(22.54, -50.17) * mm, "end": v(22.36, -48.05) * mm});
            skLineSegment(sketch, "E27.3.60.0", {"start": v(22.17, -50.33) * mm, "end": v(22.54, -50.17) * mm});
            skLineSegment(sketch, "E27.6.60.0", {"start": v(22.17, -50.33) * mm, "end": v(21.8, -50.5) * mm});
            skLineSegment(sketch, "E27.9.60.0", {"start": v(21.8, -50.5) * mm, "end": v(20.36, -48.93) * mm});
            skLineSegment(sketch, "E27.2.61.0", {"start": v(25.47, -48.75) * mm, "end": v(25.17, -46.64) * mm});
            skLineSegment(sketch, "E27.3.61.0", {"start": v(25.11, -48.93) * mm, "end": v(25.47, -48.75) * mm});
            skLineSegment(sketch, "E27.6.61.0", {"start": v(25.11, -48.93) * mm, "end": v(24.75, -49.12) * mm});
            skLineSegment(sketch, "E27.9.61.0", {"start": v(24.75, -49.12) * mm, "end": v(23.23, -47.64) * mm});
            skLineSegment(sketch, "E27.2.62.0", {"start": v(28.32, -47.15) * mm, "end": v(27.88, -45.07) * mm});
            skLineSegment(sketch, "E27.3.62.0", {"start": v(27.97, -47.36) * mm, "end": v(28.32, -47.15) * mm});
            skLineSegment(sketch, "E27.6.62.0", {"start": v(27.97, -47.36) * mm, "end": v(27.62, -47.56) * mm});
            skLineSegment(sketch, "E27.9.62.0", {"start": v(27.62, -47.56) * mm, "end": v(26, -46.18) * mm});
            skLineSegment(sketch, "E27.2.63.0", {"start": v(31.06, -45.4) * mm, "end": v(30.5, -43.34) * mm});
            skLineSegment(sketch, "E27.3.63.0", {"start": v(30.73, -45.62) * mm, "end": v(31.06, -45.4) * mm});
            skLineSegment(sketch, "E27.6.63.0", {"start": v(30.73, -45.62) * mm, "end": v(30.39, -45.84) * mm});
            skLineSegment(sketch, "E27.9.63.0", {"start": v(30.39, -45.84) * mm, "end": v(28.7, -44.56) * mm});
            skLineSegment(sketch, "E27.2.64.0", {"start": v(33.7, -43.47) * mm, "end": v(33.02, -41.46) * mm});
            skLineSegment(sketch, "E27.3.64.0", {"start": v(33.37, -43.72) * mm, "end": v(33.7, -43.47) * mm});
            skLineSegment(sketch, "E27.6.64.0", {"start": v(33.37, -43.72) * mm, "end": v(33.05, -43.96) * mm});
            skLineSegment(sketch, "E27.9.64.0", {"start": v(33.05, -43.96) * mm, "end": v(31.29, -42.78) * mm});
            skLineSegment(sketch, "E27.2.65.0", {"start": v(36.21, -41.4) * mm, "end": v(35.42, -39.43) * mm});
            skLineSegment(sketch, "E27.3.65.0", {"start": v(35.9, -41.66) * mm, "end": v(36.21, -41.4) * mm});
            skLineSegment(sketch, "E27.6.65.0", {"start": v(35.9, -41.66) * mm, "end": v(35.6, -41.93) * mm});
            skLineSegment(sketch, "E27.9.65.0", {"start": v(35.6, -41.93) * mm, "end": v(33.77, -40.85) * mm});
            skLineSegment(sketch, "E27.2.66.0", {"start": v(38.6, -39.18) * mm, "end": v(37.7, -37.26) * mm});
            skLineSegment(sketch, "E27.3.66.0", {"start": v(38.31, -39.46) * mm, "end": v(38.6, -39.18) * mm});
            skLineSegment(sketch, "E27.6.66.0", {"start": v(38.31, -39.46) * mm, "end": v(38.02, -39.75) * mm});
            skLineSegment(sketch, "E27.9.66.0", {"start": v(38.02, -39.75) * mm, "end": v(36.13, -38.78) * mm});
            skLineSegment(sketch, "E27.2.67.0", {"start": v(40.85, -36.83) * mm, "end": v(39.83, -34.96) * mm});
            skLineSegment(sketch, "E27.3.67.0", {"start": v(40.58, -37.12) * mm, "end": v(40.85, -36.83) * mm});
            skLineSegment(sketch, "E27.6.67.0", {"start": v(40.58, -37.12) * mm, "end": v(40.3, -37.42) * mm});
            skLineSegment(sketch, "E27.9.67.0", {"start": v(40.3, -37.42) * mm, "end": v(38.36, -36.57) * mm});
            skLineSegment(sketch, "E27.2.68.0", {"start": v(42.96, -34.34) * mm, "end": v(41.83, -32.54) * mm});
            skLineSegment(sketch, "E27.3.68.0", {"start": v(42.7, -34.65) * mm, "end": v(42.96, -34.34) * mm});
            skLineSegment(sketch, "E27.6.68.0", {"start": v(42.7, -34.65) * mm, "end": v(42.45, -34.97) * mm});
            skLineSegment(sketch, "E27.9.68.0", {"start": v(42.45, -34.97) * mm, "end": v(40.46, -34.23) * mm});
            skLineSegment(sketch, "E27.2.69.0", {"start": v(44.92, -31.73) * mm, "end": v(43.69, -30) * mm});
            skLineSegment(sketch, "E27.3.69.0", {"start": v(44.69, -32.06) * mm, "end": v(44.92, -31.73) * mm});
            skLineSegment(sketch, "E27.6.69.0", {"start": v(44.69, -32.06) * mm, "end": v(44.45, -32.4) * mm});
            skLineSegment(sketch, "E27.9.69.0", {"start": v(44.45, -32.4) * mm, "end": v(42.42, -31.78) * mm});
            skLineSegment(sketch, "E27.2.70.0", {"start": v(46.72, -29.02) * mm, "end": v(45.39, -27.37) * mm});
            skLineSegment(sketch, "E27.3.70.0", {"start": v(46.5, -29.36) * mm, "end": v(46.72, -29.02) * mm});
            skLineSegment(sketch, "E27.6.70.0", {"start": v(46.5, -29.36) * mm, "end": v(46.3, -29.7) * mm});
            skLineSegment(sketch, "E27.9.70.0", {"start": v(46.3, -29.7) * mm, "end": v(44.23, -29.2) * mm});
            skLineSegment(sketch, "E27.2.71.0", {"start": v(48.36, -26.2) * mm, "end": v(46.93, -24.63) * mm});
            skLineSegment(sketch, "E27.3.71.0", {"start": v(48.17, -26.55) * mm, "end": v(48.36, -26.2) * mm});
            skLineSegment(sketch, "E27.6.71.0", {"start": v(48.17, -26.55) * mm, "end": v(47.97, -26.9) * mm});
            skLineSegment(sketch, "E27.9.71.0", {"start": v(47.97, -26.9) * mm, "end": v(45.88, -26.54) * mm});
            skLineSegment(sketch, "E27.2.72.0", {"start": v(49.83, -23.29) * mm, "end": v(48.3, -21.8) * mm});
            skLineSegment(sketch, "E27.3.72.0", {"start": v(49.65, -23.65) * mm, "end": v(49.83, -23.29) * mm});
            skLineSegment(sketch, "E27.6.72.0", {"start": v(49.65, -23.65) * mm, "end": v(49.48, -24.02) * mm});
            skLineSegment(sketch, "E27.9.72.0", {"start": v(49.48, -24.02) * mm, "end": v(47.37, -23.77) * mm});
            skLineSegment(sketch, "E27.2.73.0", {"start": v(51.12, -20.3) * mm, "end": v(49.51, -18.9) * mm});
            skLineSegment(sketch, "E27.3.73.0", {"start": v(50.97, -20.67) * mm, "end": v(51.12, -20.3) * mm});
            skLineSegment(sketch, "E27.6.73.0", {"start": v(50.97, -20.67) * mm, "end": v(50.82, -21.05) * mm});
            skLineSegment(sketch, "E27.9.73.0", {"start": v(50.82, -21.05) * mm, "end": v(48.7, -20.92) * mm});
            skLineSegment(sketch, "E27.2.74.0", {"start": v(52.23, -17.23) * mm, "end": v(50.55, -15.94) * mm});
            skLineSegment(sketch, "E27.3.74.0", {"start": v(52.1, -17.61) * mm, "end": v(52.23, -17.23) * mm});
            skLineSegment(sketch, "E27.6.74.0", {"start": v(52.1, -17.61) * mm, "end": v(51.97, -18) * mm});
            skLineSegment(sketch, "E27.9.74.0", {"start": v(51.97, -18) * mm, "end": v(49.85, -18) * mm});
            skLineSegment(sketch, "E27.2.75.0", {"start": v(53.16, -14.1) * mm, "end": v(51.4, -12.92) * mm});
            skLineSegment(sketch, "E27.3.75.0", {"start": v(53.05, -14.5) * mm, "end": v(53.16, -14.1) * mm});
            skLineSegment(sketch, "E27.6.75.0", {"start": v(53.05, -14.5) * mm, "end": v(52.95, -14.89) * mm});
            skLineSegment(sketch, "E27.9.75.0", {"start": v(52.95, -14.89) * mm, "end": v(50.83, -15.02) * mm});
            skLineSegment(sketch, "E27.2.76.0", {"start": v(53.9, -10.93) * mm, "end": v(52.08, -9.85) * mm});
            skLineSegment(sketch, "E27.3.76.0", {"start": v(53.82, -11.33) * mm, "end": v(53.9, -10.93) * mm});
            skLineSegment(sketch, "E27.6.76.0", {"start": v(53.82, -11.33) * mm, "end": v(53.74, -11.73) * mm});
            skLineSegment(sketch, "E27.9.76.0", {"start": v(53.74, -11.73) * mm, "end": v(51.63, -11.98) * mm});
            skLineSegment(sketch, "E27.2.77.0", {"start": v(54.46, -7.72) * mm, "end": v(52.57, -6.75) * mm});
            skLineSegment(sketch, "E27.3.77.0", {"start": v(54.4, -8.12) * mm, "end": v(54.46, -7.72) * mm});
            skLineSegment(sketch, "E27.6.77.0", {"start": v(54.4, -8.12) * mm, "end": v(54.34, -8.52) * mm});
            skLineSegment(sketch, "E27.9.77.0", {"start": v(54.34, -8.52) * mm, "end": v(52.25, -8.9) * mm});
            skLineSegment(sketch, "E27.2.78.0", {"start": v(54.82, -4.48) * mm, "end": v(52.88, -3.62) * mm});
            skLineSegment(sketch, "E27.3.78.0", {"start": v(54.78, -4.88) * mm, "end": v(54.82, -4.48) * mm});
            skLineSegment(sketch, "E27.6.78.0", {"start": v(54.78, -4.88) * mm, "end": v(54.75, -5.29) * mm});
            skLineSegment(sketch, "E27.9.78.0", {"start": v(54.75, -5.29) * mm, "end": v(52.68, -5.8) * mm});
            skLineSegment(sketch, "E27.2.79.0", {"start": v(54.99, -1.23) * mm, "end": v(53, -0.48) * mm});
            skLineSegment(sketch, "E27.3.79.0", {"start": v(54.98, -1.63) * mm, "end": v(54.99, -1.23) * mm});
            skLineSegment(sketch, "E27.6.79.0", {"start": v(54.98, -1.63) * mm, "end": v(54.96, -2.03) * mm});
            skLineSegment(sketch, "E27.9.79.0", {"start": v(54.96, -2.03) * mm, "end": v(52.93, -2.66) * mm});
            skLineSegment(sketch, "E27.2.80.0", {"start": v(54.96, 2.03) * mm, "end": v(52.93, 2.66) * mm});
            skLineSegment(sketch, "E27.3.80.0", {"start": v(54.98, 1.63) * mm, "end": v(54.96, 2.03) * mm});
            skLineSegment(sketch, "E27.6.80.0", {"start": v(54.98, 1.63) * mm, "end": v(54.99, 1.23) * mm});
            skLineSegment(sketch, "E27.9.80.0", {"start": v(54.99, 1.23) * mm, "end": v(53, 0.48) * mm});
            skLineSegment(sketch, "E27.2.81.0", {"start": v(54.75, 5.29) * mm, "end": v(52.68, 5.8) * mm});
            skLineSegment(sketch, "E27.3.81.0", {"start": v(54.78, 4.88) * mm, "end": v(54.75, 5.29) * mm});
            skLineSegment(sketch, "E27.6.81.0", {"start": v(54.78, 4.88) * mm, "end": v(54.82, 4.48) * mm});
            skLineSegment(sketch, "E27.9.81.0", {"start": v(54.82, 4.48) * mm, "end": v(52.88, 3.62) * mm});
            skLineSegment(sketch, "E27.2.82.0", {"start": v(54.34, 8.52) * mm, "end": v(52.25, 8.9) * mm});
            skLineSegment(sketch, "E27.3.82.0", {"start": v(54.4, 8.12) * mm, "end": v(54.34, 8.52) * mm});
            skLineSegment(sketch, "E27.6.82.0", {"start": v(54.4, 8.12) * mm, "end": v(54.46, 7.72) * mm});
            skLineSegment(sketch, "E27.9.82.0", {"start": v(54.46, 7.72) * mm, "end": v(52.57, 6.75) * mm});
            skLineSegment(sketch, "E27.2.83.0", {"start": v(53.74, 11.73) * mm, "end": v(51.63, 11.98) * mm});
            skLineSegment(sketch, "E27.3.83.0", {"start": v(53.82, 11.33) * mm, "end": v(53.74, 11.73) * mm});
            skLineSegment(sketch, "E27.6.83.0", {"start": v(53.82, 11.33) * mm, "end": v(53.9, 10.93) * mm});
            skLineSegment(sketch, "E27.9.83.0", {"start": v(53.9, 10.93) * mm, "end": v(52.08, 9.85) * mm});
            skLineSegment(sketch, "E27.2.84.0", {"start": v(52.95, 14.89) * mm, "end": v(50.83, 15.02) * mm});
            skLineSegment(sketch, "E27.3.84.0", {"start": v(53.05, 14.5) * mm, "end": v(52.95, 14.89) * mm});
            skLineSegment(sketch, "E27.6.84.0", {"start": v(53.05, 14.5) * mm, "end": v(53.16, 14.1) * mm});
            skLineSegment(sketch, "E27.9.84.0", {"start": v(53.16, 14.1) * mm, "end": v(51.4, 12.92) * mm});
            skLineSegment(sketch, "E27.2.85.0", {"start": v(51.97, 18) * mm, "end": v(49.85, 18) * mm});
            skLineSegment(sketch, "E27.3.85.0", {"start": v(52.1, 17.61) * mm, "end": v(51.97, 18) * mm});
            skLineSegment(sketch, "E27.6.85.0", {"start": v(52.1, 17.61) * mm, "end": v(52.23, 17.23) * mm});
            skLineSegment(sketch, "E27.9.85.0", {"start": v(52.23, 17.23) * mm, "end": v(50.55, 15.94) * mm});
            skLineSegment(sketch, "E27.2.86.0", {"start": v(50.82, 21.05) * mm, "end": v(48.7, 20.92) * mm});
            skLineSegment(sketch, "E27.3.86.0", {"start": v(50.97, 20.67) * mm, "end": v(50.82, 21.05) * mm});
            skLineSegment(sketch, "E27.6.86.0", {"start": v(50.97, 20.67) * mm, "end": v(51.12, 20.3) * mm});
            skLineSegment(sketch, "E27.9.86.0", {"start": v(51.12, 20.3) * mm, "end": v(49.51, 18.9) * mm});
            skLineSegment(sketch, "E27.2.87.0", {"start": v(49.48, 24.02) * mm, "end": v(47.37, 23.77) * mm});
            skLineSegment(sketch, "E27.3.87.0", {"start": v(49.65, 23.65) * mm, "end": v(49.48, 24.02) * mm});
            skLineSegment(sketch, "E27.6.87.0", {"start": v(49.65, 23.65) * mm, "end": v(49.83, 23.29) * mm});
            skLineSegment(sketch, "E27.9.87.0", {"start": v(49.83, 23.29) * mm, "end": v(48.3, 21.8) * mm});
            skLineSegment(sketch, "E27.2.88.0", {"start": v(47.97, 26.9) * mm, "end": v(45.88, 26.54) * mm});
            skLineSegment(sketch, "E27.3.88.0", {"start": v(48.17, 26.55) * mm, "end": v(47.97, 26.9) * mm});
            skLineSegment(sketch, "E27.6.88.0", {"start": v(48.17, 26.55) * mm, "end": v(48.36, 26.2) * mm});
            skLineSegment(sketch, "E27.9.88.0", {"start": v(48.36, 26.2) * mm, "end": v(46.93, 24.63) * mm});
            skLineSegment(sketch, "E27.2.89.0", {"start": v(46.3, 29.7) * mm, "end": v(44.23, 29.2) * mm});
            skLineSegment(sketch, "E27.3.89.0", {"start": v(46.5, 29.36) * mm, "end": v(46.3, 29.7) * mm});
            skLineSegment(sketch, "E27.6.89.0", {"start": v(46.5, 29.36) * mm, "end": v(46.72, 29.02) * mm});
            skLineSegment(sketch, "E27.9.89.0", {"start": v(46.72, 29.02) * mm, "end": v(45.39, 27.37) * mm});
            skLineSegment(sketch, "E27.2.90.0", {"start": v(44.45, 32.4) * mm, "end": v(42.42, 31.78) * mm});
            skLineSegment(sketch, "E27.3.90.0", {"start": v(44.69, 32.06) * mm, "end": v(44.45, 32.4) * mm});
            skLineSegment(sketch, "E27.6.90.0", {"start": v(44.69, 32.06) * mm, "end": v(44.92, 31.73) * mm});
            skLineSegment(sketch, "E27.9.90.0", {"start": v(44.92, 31.73) * mm, "end": v(43.69, 30) * mm});
            skLineSegment(sketch, "E27.2.91.0", {"start": v(42.45, 34.97) * mm, "end": v(40.46, 34.23) * mm});
            skLineSegment(sketch, "E27.3.91.0", {"start": v(42.7, 34.65) * mm, "end": v(42.45, 34.97) * mm});
            skLineSegment(sketch, "E27.6.91.0", {"start": v(42.7, 34.65) * mm, "end": v(42.96, 34.34) * mm});
            skLineSegment(sketch, "E27.9.91.0", {"start": v(42.96, 34.34) * mm, "end": v(41.83, 32.54) * mm});
            skLineSegment(sketch, "E27.2.92.0", {"start": v(40.3, 37.42) * mm, "end": v(38.36, 36.57) * mm});
            skLineSegment(sketch, "E27.3.92.0", {"start": v(40.58, 37.12) * mm, "end": v(40.3, 37.42) * mm});
            skLineSegment(sketch, "E27.6.92.0", {"start": v(40.58, 37.12) * mm, "end": v(40.85, 36.83) * mm});
            skLineSegment(sketch, "E27.9.92.0", {"start": v(40.85, 36.83) * mm, "end": v(39.83, 34.96) * mm});
            skLineSegment(sketch, "E27.2.93.0", {"start": v(38.02, 39.75) * mm, "end": v(36.13, 38.78) * mm});
            skLineSegment(sketch, "E27.3.93.0", {"start": v(38.31, 39.46) * mm, "end": v(38.02, 39.75) * mm});
            skLineSegment(sketch, "E27.6.93.0", {"start": v(38.31, 39.46) * mm, "end": v(38.6, 39.18) * mm});
            skLineSegment(sketch, "E27.9.93.0", {"start": v(38.6, 39.18) * mm, "end": v(37.7, 37.26) * mm});
            skLineSegment(sketch, "E27.2.94.0", {"start": v(35.6, 41.93) * mm, "end": v(33.77, 40.85) * mm});
            skLineSegment(sketch, "E27.3.94.0", {"start": v(35.9, 41.66) * mm, "end": v(35.6, 41.93) * mm});
            skLineSegment(sketch, "E27.6.94.0", {"start": v(35.9, 41.66) * mm, "end": v(36.21, 41.4) * mm});
            skLineSegment(sketch, "E27.9.94.0", {"start": v(36.21, 41.4) * mm, "end": v(35.42, 39.43) * mm});
            skLineSegment(sketch, "E27.2.95.0", {"start": v(33.05, 43.96) * mm, "end": v(31.29, 42.78) * mm});
            skLineSegment(sketch, "E27.3.95.0", {"start": v(33.37, 43.72) * mm, "end": v(33.05, 43.96) * mm});
            skLineSegment(sketch, "E27.6.95.0", {"start": v(33.37, 43.72) * mm, "end": v(33.7, 43.47) * mm});
            skLineSegment(sketch, "E27.9.95.0", {"start": v(33.7, 43.47) * mm, "end": v(33.02, 41.46) * mm});
            skLineSegment(sketch, "E27.2.96.0", {"start": v(30.39, 45.84) * mm, "end": v(28.7, 44.56) * mm});
            skLineSegment(sketch, "E27.3.96.0", {"start": v(30.73, 45.62) * mm, "end": v(30.39, 45.84) * mm});
            skLineSegment(sketch, "E27.6.96.0", {"start": v(30.73, 45.62) * mm, "end": v(31.06, 45.4) * mm});
            skLineSegment(sketch, "E27.9.96.0", {"start": v(31.06, 45.4) * mm, "end": v(30.5, 43.34) * mm});
            skLineSegment(sketch, "E27.2.97.0", {"start": v(27.62, 47.56) * mm, "end": v(26, 46.18) * mm});
            skLineSegment(sketch, "E27.3.97.0", {"start": v(27.97, 47.36) * mm, "end": v(27.62, 47.56) * mm});
            skLineSegment(sketch, "E27.6.97.0", {"start": v(27.97, 47.36) * mm, "end": v(28.32, 47.15) * mm});
            skLineSegment(sketch, "E27.9.97.0", {"start": v(28.32, 47.15) * mm, "end": v(27.88, 45.07) * mm});
            skLineSegment(sketch, "E27.2.98.0", {"start": v(24.75, 49.12) * mm, "end": v(23.23, 47.64) * mm});
            skLineSegment(sketch, "E27.3.98.0", {"start": v(25.11, 48.93) * mm, "end": v(24.75, 49.12) * mm});
            skLineSegment(sketch, "E27.6.98.0", {"start": v(25.11, 48.93) * mm, "end": v(25.47, 48.75) * mm});
            skLineSegment(sketch, "E27.9.98.0", {"start": v(25.47, 48.75) * mm, "end": v(25.17, 46.64) * mm});
            skLineSegment(sketch, "E27.2.99.0", {"start": v(21.8, 50.5) * mm, "end": v(20.36, 48.93) * mm});
            skLineSegment(sketch, "E27.3.99.0", {"start": v(22.17, 50.33) * mm, "end": v(21.8, 50.5) * mm});
            skLineSegment(sketch, "E27.6.99.0", {"start": v(22.17, 50.33) * mm, "end": v(22.54, 50.17) * mm});
            skLineSegment(sketch, "E27.9.99.0", {"start": v(22.54, 50.17) * mm, "end": v(22.36, 48.05) * mm});
            skLineSegment(sketch, "E27.2.100.0", {"start": v(18.77, 51.7) * mm, "end": v(17.43, 50.05) * mm});
            skLineSegment(sketch, "E27.3.100.0", {"start": v(19.15, 51.56) * mm, "end": v(18.77, 51.7) * mm});
            skLineSegment(sketch, "E27.6.100.0", {"start": v(19.15, 51.56) * mm, "end": v(19.53, 51.42) * mm});
            skLineSegment(sketch, "E27.9.100.0", {"start": v(19.53, 51.42) * mm, "end": v(19.47, 49.3) * mm});
            skLineSegment(sketch, "E27.2.101.0", {"start": v(15.68, 52.72) * mm, "end": v(14.43, 51) * mm});
            skLineSegment(sketch, "E27.3.101.0", {"start": v(16.06, 52.6) * mm, "end": v(15.68, 52.72) * mm});
            skLineSegment(sketch, "E27.6.101.0", {"start": v(16.06, 52.6) * mm, "end": v(16.45, 52.48) * mm});
            skLineSegment(sketch, "E27.9.101.0", {"start": v(16.45, 52.48) * mm, "end": v(16.52, 50.36) * mm});
            skLineSegment(sketch, "E27.2.102.0", {"start": v(12.53, 53.56) * mm, "end": v(11.39, 51.76) * mm});
            skLineSegment(sketch, "E27.3.102.0", {"start": v(12.92, 53.46) * mm, "end": v(12.53, 53.56) * mm});
            skLineSegment(sketch, "E27.6.102.0", {"start": v(12.92, 53.46) * mm, "end": v(13.31, 53.37) * mm});
            skLineSegment(sketch, "E27.9.102.0", {"start": v(13.31, 53.37) * mm, "end": v(13.5, 51.25) * mm});
            skLineSegment(sketch, "E27.2.103.0", {"start": v(9.33, 54.2) * mm, "end": v(8.3, 52.35) * mm});
            skLineSegment(sketch, "E27.3.103.0", {"start": v(9.73, 54.13) * mm, "end": v(9.33, 54.2) * mm});
            skLineSegment(sketch, "E27.6.103.0", {"start": v(9.73, 54.13) * mm, "end": v(10.13, 54.06) * mm});
            skLineSegment(sketch, "E27.9.103.0", {"start": v(10.13, 54.06) * mm, "end": v(10.45, 51.96) * mm});
            skLineSegment(sketch, "E27.2.104.0", {"start": v(6.1, 54.66) * mm, "end": v(5.19, 52.75) * mm});
            skLineSegment(sketch, "E27.3.104.0", {"start": v(6.5, 54.61) * mm, "end": v(6.1, 54.66) * mm});
            skLineSegment(sketch, "E27.6.104.0", {"start": v(6.5, 54.61) * mm, "end": v(6.9, 54.57) * mm});
            skLineSegment(sketch, "E27.9.104.0", {"start": v(6.9, 54.57) * mm, "end": v(7.35, 52.49) * mm});
            skLineSegment(sketch, "E27.2.105.0", {"start": v(2.85, 54.93) * mm, "end": v(2.05, 52.96) * mm});
            skLineSegment(sketch, "E27.3.105.0", {"start": v(3.26, 54.9) * mm, "end": v(2.85, 54.93) * mm});
            skLineSegment(sketch, "E27.6.105.0", {"start": v(3.26, 54.9) * mm, "end": v(3.66, 54.88) * mm});
            skLineSegment(sketch, "E27.9.105.0", {"start": v(3.66, 54.88) * mm, "end": v(4.23, 52.83) * mm});
            skSolve(sketch);
        }
        {
            var Q0;
            Q0=makeQuery(id+"F0.imprint","IMPRINT",FACE,{"disambiguationData":[TD([[makeQuery(id+"F0.imprint","IMPRINT",EDGE,{"derivedFrom":sQuery(id+"F0.wireOp",EDGE,"E4")}),-1.0]])]});
            var Q1;
            Q1=makeQuery(id+"F0.imprint","IMPRINT",FACE,{"disambiguationData":[TD([[makeQuery(id+"F0.imprint","IMPRINT",EDGE,{"derivedFrom":sQuery(id+"F0.wireOp",EDGE,"E6")}),1.0]])]});
            var Q2;
            {var subQ0=sQuery(id+"F0.wireOp",EDGE,"E16.MirrorC");var subQ1=sQuery(id+"F0.wireOp",EDGE,"E5");var subQ2=makeQuery(id+"F0.imprint","INTERSECT",VERTEX,{"disambiguationData":[OD(0.0)],"derivedFrom":[subQ1,subQ0]});Q2=makeQuery(id+"F0.imprint","IMPRINT",FACE,{"disambiguationData":[TD([[makeQuery(id+"F0.imprint","IMPRINT",EDGE,{"disambiguationData":[TD([[subQ2,-1.0]])],"derivedFrom":subQ1}),-1.0]])]});}
            var Q3;
            {var subQ0=sQuery(id+"F0.wireOp",EDGE,"E16.MirrorC");var subQ1=sQuery(id+"F0.wireOp",EDGE,"E5");var subQ2=makeQuery(id+"F0.imprint","INTERSECT",VERTEX,{"disambiguationData":[OD(0.0)],"derivedFrom":[subQ1,subQ0]});Q3=makeQuery(id+"F0.imprint","IMPRINT",FACE,{"disambiguationData":[TD([[makeQuery(id+"F0.imprint","IMPRINT",EDGE,{"disambiguationData":[TD([[subQ2,-1.0]])],"derivedFrom":subQ1}),1.0]])]});}
            var Q4;
            {var subQ0=sQuery(id+"F0.wireOp",EDGE,"E18");var subQ1=sQuery(id+"F0.wireOp",EDGE,"E5");var subQ2=makeQuery(id+"F0.imprint","INTERSECT",VERTEX,{"disambiguationData":[OD(0.0)],"derivedFrom":[subQ1,subQ0]});Q4=makeQuery(id+"F0.imprint","IMPRINT",FACE,{"disambiguationData":[TD([[makeQuery(id+"F0.imprint","IMPRINT",EDGE,{"disambiguationData":[TD([[subQ2,-1.0]])],"derivedFrom":subQ1}),-1.0]])]});}
            var Q5;
            {var subQ0=sQuery(id+"F0.wireOp",EDGE,"E18");var subQ1=sQuery(id+"F0.wireOp",EDGE,"E5");var subQ2=makeQuery(id+"F0.imprint","INTERSECT",VERTEX,{"disambiguationData":[OD(0.0)],"derivedFrom":[subQ1,subQ0]});Q5=makeQuery(id+"F0.imprint","IMPRINT",FACE,{"disambiguationData":[TD([[makeQuery(id+"F0.imprint","IMPRINT",EDGE,{"disambiguationData":[TD([[subQ2,-1.0]])],"derivedFrom":subQ1}),1.0]])]});}
            var Q6;
            {var subQ0=sQuery(id+"F0.wireOp",EDGE,"E21");var subQ1=sQuery(id+"F0.wireOp",EDGE,"E5");var subQ2=makeQuery(id+"F0.imprint","INTERSECT",VERTEX,{"disambiguationData":[OD(0.0)],"derivedFrom":[subQ1,subQ0]});Q6=makeQuery(id+"F0.imprint","IMPRINT",FACE,{"disambiguationData":[TD([[makeQuery(id+"F0.imprint","IMPRINT",EDGE,{"disambiguationData":[TD([[subQ2,-1.0]])],"derivedFrom":subQ1}),-1.0]])]});}
            var Q7;
            {var subQ0=sQuery(id+"F0.wireOp",EDGE,"E21");var subQ1=sQuery(id+"F0.wireOp",EDGE,"E5");var subQ2=makeQuery(id+"F0.imprint","INTERSECT",VERTEX,{"disambiguationData":[OD(0.0)],"derivedFrom":[subQ1,subQ0]});Q7=makeQuery(id+"F0.imprint","IMPRINT",FACE,{"disambiguationData":[TD([[makeQuery(id+"F0.imprint","IMPRINT",EDGE,{"disambiguationData":[TD([[subQ2,-1.0]])],"derivedFrom":subQ1}),1.0]])]});}
            var Q8;
            {var subQ0=sQuery(id+"F0.wireOp",EDGE,"E13");var subQ1=sQuery(id+"F0.wireOp",EDGE,"E5");var subQ2=makeQuery(id+"F0.imprint","INTERSECT",VERTEX,{"disambiguationData":[OD(0.0)],"derivedFrom":[subQ1,subQ0]});Q8=makeQuery(id+"F0.imprint","IMPRINT",FACE,{"disambiguationData":[TD([[makeQuery(id+"F0.imprint","IMPRINT",EDGE,{"disambiguationData":[TD([[subQ2,-1.0]])],"derivedFrom":subQ1}),-1.0]])]});}
            var Q9;
            {var subQ0=sQuery(id+"F0.wireOp",EDGE,"E13");var subQ1=sQuery(id+"F0.wireOp",EDGE,"E5");var subQ2=makeQuery(id+"F0.imprint","INTERSECT",VERTEX,{"disambiguationData":[OD(0.0)],"derivedFrom":[subQ1,subQ0]});Q9=makeQuery(id+"F0.imprint","IMPRINT",FACE,{"disambiguationData":[TD([[makeQuery(id+"F0.imprint","IMPRINT",EDGE,{"disambiguationData":[TD([[subQ2,-1.0]])],"derivedFrom":subQ1}),1.0]])]});}
            var Q10;
            {var subQ0=sQuery(id+"F0.wireOp",EDGE,"E12");var subQ1=sQuery(id+"F0.wireOp",EDGE,"E5");var subQ2=makeQuery(id+"F0.imprint","INTERSECT",VERTEX,{"disambiguationData":[OD(0.0)],"derivedFrom":[subQ1,subQ0]});Q10=makeQuery(id+"F0.imprint","IMPRINT",FACE,{"disambiguationData":[TD([[makeQuery(id+"F0.imprint","IMPRINT",EDGE,{"disambiguationData":[TD([[subQ2,1.0]])],"derivedFrom":subQ1}),-1.0]])]});}
            var Q11;
            {var subQ0=sQuery(id+"F0.wireOp",EDGE,"E12");var subQ1=sQuery(id+"F0.wireOp",EDGE,"E5");var subQ2=makeQuery(id+"F0.imprint","INTERSECT",VERTEX,{"disambiguationData":[OD(0.0)],"derivedFrom":[subQ1,subQ0]});Q11=makeQuery(id+"F0.imprint","IMPRINT",FACE,{"disambiguationData":[TD([[makeQuery(id+"F0.imprint","IMPRINT",EDGE,{"disambiguationData":[TD([[subQ2,1.0]])],"derivedFrom":subQ1}),1.0]])]});}
            var Q12;
            {var subQ0=sQuery(id+"F0.wireOp",EDGE,"E22");var subQ1=sQuery(id+"F0.wireOp",EDGE,"E5");var subQ2=makeQuery(id+"F0.imprint","INTERSECT",VERTEX,{"disambiguationData":[OD(0.0)],"derivedFrom":[subQ1,subQ0]});Q12=makeQuery(id+"F0.imprint","IMPRINT",FACE,{"disambiguationData":[TD([[makeQuery(id+"F0.imprint","IMPRINT",EDGE,{"disambiguationData":[TD([[subQ2,-1.0]])],"derivedFrom":subQ1}),1.0]])]});}
            var Q13;
            {var subQ0=sQuery(id+"F0.wireOp",EDGE,"E22");var subQ1=sQuery(id+"F0.wireOp",EDGE,"E5");var subQ2=makeQuery(id+"F0.imprint","INTERSECT",VERTEX,{"disambiguationData":[OD(0.0)],"derivedFrom":[subQ1,subQ0]});Q13=makeQuery(id+"F0.imprint","IMPRINT",FACE,{"disambiguationData":[TD([[makeQuery(id+"F0.imprint","IMPRINT",EDGE,{"disambiguationData":[TD([[subQ2,-1.0]])],"derivedFrom":subQ1}),-1.0]])]});}
            var Q14;
            {var subQ0=sQuery(id+"F0.wireOp",EDGE,"E11");var subQ1=sQuery(id+"F0.wireOp",EDGE,"E5");var subQ2=makeQuery(id+"F0.imprint","INTERSECT",VERTEX,{"disambiguationData":[OD(0.0)],"derivedFrom":[subQ1,subQ0]});Q14=makeQuery(id+"F0.imprint","IMPRINT",FACE,{"disambiguationData":[TD([[makeQuery(id+"F0.imprint","IMPRINT",EDGE,{"disambiguationData":[TD([[subQ2,-1.0]])],"derivedFrom":subQ1}),1.0]])]});}
            var Q15;
            {var subQ0=sQuery(id+"F0.wireOp",EDGE,"E11");var subQ1=sQuery(id+"F0.wireOp",EDGE,"E5");var subQ2=makeQuery(id+"F0.imprint","INTERSECT",VERTEX,{"disambiguationData":[OD(0.0)],"derivedFrom":[subQ1,subQ0]});Q15=makeQuery(id+"F0.imprint","IMPRINT",FACE,{"disambiguationData":[TD([[makeQuery(id+"F0.imprint","IMPRINT",EDGE,{"disambiguationData":[TD([[subQ2,-1.0]])],"derivedFrom":subQ1}),-1.0]])]});}
            var Q16;
            {var subQ0=sQuery(id+"F0.wireOp",EDGE,"E20.MirrorC");var subQ1=sQuery(id+"F0.wireOp",EDGE,"E5");var subQ2=makeQuery(id+"F0.imprint","INTERSECT",VERTEX,{"disambiguationData":[OD(0.0)],"derivedFrom":[subQ1,subQ0]});Q16=makeQuery(id+"F0.imprint","IMPRINT",FACE,{"disambiguationData":[TD([[makeQuery(id+"F0.imprint","IMPRINT",EDGE,{"disambiguationData":[TD([[subQ2,-1.0]])],"derivedFrom":subQ1}),1.0]])]});}
            var Q17;
            {var subQ0=sQuery(id+"F0.wireOp",EDGE,"E20.MirrorC");var subQ1=sQuery(id+"F0.wireOp",EDGE,"E5");var subQ2=makeQuery(id+"F0.imprint","INTERSECT",VERTEX,{"disambiguationData":[OD(0.0)],"derivedFrom":[subQ1,subQ0]});Q17=makeQuery(id+"F0.imprint","IMPRINT",FACE,{"disambiguationData":[TD([[makeQuery(id+"F0.imprint","IMPRINT",EDGE,{"disambiguationData":[TD([[subQ2,-1.0]])],"derivedFrom":subQ1}),-1.0]])]});}
            var Q18;
            Q18=makeQuery(id+"F0.imprint","IMPRINT",FACE,{"disambiguationData":[TD([[makeQuery(id+"F0.imprint","IMPRINT",EDGE,{"derivedFrom":sQuery(id+"F0.wireOp",EDGE,"E6")}),-1.0]])]});
            extrude(context, id + "F1", {"entities" : qUnion([Q0, Q1, Q2, Q3, Q4, Q5, Q6, Q7, Q8, Q9, Q10, Q11, Q12, Q13, Q14, Q15, Q16, Q17, Q18]), "depth" : 3 * mm, "offsetDistance" : 25 * mm});
        }
        {
            var Q0;
            Q0=makeQuery(id+"F0.imprint","IMPRINT",FACE,{"disambiguationData":[TD([[makeQuery(id+"F0.imprint","IMPRINT",EDGE,{"derivedFrom":sQuery(id+"F0.wireOp",EDGE,"E7")}),-1.0]])]});
            var Q1;
            Q1=makeQuery(id+"F0.imprint","IMPRINT",FACE,{"disambiguationData":[TD([[makeQuery(id+"F0.imprint","IMPRINT",EDGE,{"derivedFrom":sQuery(id+"F0.wireOp",EDGE,"E1")}),1.0]])]});
            var Q2;
            {var subQ2=sQuery(id+"F0.wireOp",EDGE,"E26.1.0");Q2=makeQuery(id+"F0.imprint","IMPRINT",FACE,{"disambiguationData":[TD([[makeQuery(id+"F0.imprint","IMPRINT",EDGE,{"derivedFrom":subQ2}),1.0]])]});}
            var Q3;
            {var subQ1=sQuery(id+"F0.wireOp",EDGE,"E26.3.0");Q3=makeQuery(id+"F0.imprint","IMPRINT",FACE,{"disambiguationData":[TD([[makeQuery(id+"F0.imprint","IMPRINT",EDGE,{"derivedFrom":subQ1}),1.0]])]});}
            var Q4;
            {var subQ2=sQuery(id+"F0.wireOp",EDGE,"E26.2.0");Q4=makeQuery(id+"F0.imprint","IMPRINT",FACE,{"disambiguationData":[TD([[makeQuery(id+"F0.imprint","IMPRINT",EDGE,{"derivedFrom":subQ2}),1.0]])]});}
            var Q5;
            {var subQ1=sQuery(id+"F0.wireOp",EDGE,"E26.4.0");Q5=makeQuery(id+"F0.imprint","IMPRINT",FACE,{"disambiguationData":[TD([[makeQuery(id+"F0.imprint","IMPRINT",EDGE,{"derivedFrom":subQ1}),1.0]])]});}
            var Q6;
            {var subQ1=sQuery(id+"F0.wireOp",EDGE,"E26.5.0");Q6=makeQuery(id+"F0.imprint","IMPRINT",FACE,{"disambiguationData":[TD([[makeQuery(id+"F0.imprint","IMPRINT",EDGE,{"derivedFrom":subQ1}),1.0]])]});}
            var Q7;
            {var subQ1=sQuery(id+"F0.wireOp",EDGE,"E26.6.0");Q7=makeQuery(id+"F0.imprint","IMPRINT",FACE,{"disambiguationData":[TD([[makeQuery(id+"F0.imprint","IMPRINT",EDGE,{"derivedFrom":subQ1}),1.0]])]});}
            var Q8;
            {var subQ2=sQuery(id+"F0.wireOp",EDGE,"E26.7.0");Q8=makeQuery(id+"F0.imprint","IMPRINT",FACE,{"disambiguationData":[TD([[makeQuery(id+"F0.imprint","IMPRINT",EDGE,{"derivedFrom":subQ2}),1.0]])]});}
            var Q9;
            {var subQ1=sQuery(id+"F0.wireOp",EDGE,"E26.9.0");Q9=makeQuery(id+"F0.imprint","IMPRINT",FACE,{"disambiguationData":[TD([[makeQuery(id+"F0.imprint","IMPRINT",EDGE,{"derivedFrom":subQ1}),1.0]])]});}
            var Q10;
            {var subQ1=sQuery(id+"F0.wireOp",EDGE,"E26.8.0");Q10=makeQuery(id+"F0.imprint","IMPRINT",FACE,{"disambiguationData":[TD([[makeQuery(id+"F0.imprint","IMPRINT",EDGE,{"derivedFrom":subQ1}),1.0]])]});}
            var Q11;
            {var subQ1=sQuery(id+"F0.wireOp",EDGE,"E26.10.0");Q11=makeQuery(id+"F0.imprint","IMPRINT",FACE,{"disambiguationData":[TD([[makeQuery(id+"F0.imprint","IMPRINT",EDGE,{"derivedFrom":subQ1}),1.0]])]});}
            var Q12;
            {var subQ1=sQuery(id+"F0.wireOp",EDGE,"E26.11.0");Q12=makeQuery(id+"F0.imprint","IMPRINT",FACE,{"disambiguationData":[TD([[makeQuery(id+"F0.imprint","IMPRINT",EDGE,{"derivedFrom":subQ1}),1.0]])]});}
            var Q13;
            {var subQ2=sQuery(id+"F0.wireOp",EDGE,"E26.12.0");Q13=makeQuery(id+"F0.imprint","IMPRINT",FACE,{"disambiguationData":[TD([[makeQuery(id+"F0.imprint","IMPRINT",EDGE,{"derivedFrom":subQ2}),1.0]])]});}
            var Q14;
            {var subQ2=sQuery(id+"F0.wireOp",EDGE,"E26.13.0");Q14=makeQuery(id+"F0.imprint","IMPRINT",FACE,{"disambiguationData":[TD([[makeQuery(id+"F0.imprint","IMPRINT",EDGE,{"derivedFrom":subQ2}),1.0]])]});}
            var Q15;
            {var subQ1=sQuery(id+"F0.wireOp",EDGE,"E26.14.0");Q15=makeQuery(id+"F0.imprint","IMPRINT",FACE,{"disambiguationData":[TD([[makeQuery(id+"F0.imprint","IMPRINT",EDGE,{"derivedFrom":subQ1}),1.0]])]});}
            var Q16;
            {var subQ1=sQuery(id+"F0.wireOp",EDGE,"E26.15.0");Q16=makeQuery(id+"F0.imprint","IMPRINT",FACE,{"disambiguationData":[TD([[makeQuery(id+"F0.imprint","IMPRINT",EDGE,{"derivedFrom":subQ1}),1.0]])]});}
            var Q17;
            {var subQ1=sQuery(id+"F0.wireOp",EDGE,"E27.2.16.0");Q17=makeQuery(id+"F0.imprint","IMPRINT",FACE,{"disambiguationData":[TD([[makeQuery(id+"F0.imprint","IMPRINT",EDGE,{"derivedFrom":subQ1}),1.0]])]});}
            var Q18;
            {var subQ1=sQuery(id+"F0.wireOp",EDGE,"E27.2.17.0");Q18=makeQuery(id+"F0.imprint","IMPRINT",FACE,{"disambiguationData":[TD([[makeQuery(id+"F0.imprint","IMPRINT",EDGE,{"derivedFrom":subQ1}),1.0]])]});}
            var Q19;
            {var subQ1=sQuery(id+"F0.wireOp",EDGE,"E27.2.21.0");Q19=makeQuery(id+"F0.imprint","IMPRINT",FACE,{"disambiguationData":[TD([[makeQuery(id+"F0.imprint","IMPRINT",EDGE,{"derivedFrom":subQ1}),1.0]])]});}
            var Q20;
            {var subQ2=sQuery(id+"F0.wireOp",EDGE,"E27.2.18.0");Q20=makeQuery(id+"F0.imprint","IMPRINT",FACE,{"disambiguationData":[TD([[makeQuery(id+"F0.imprint","IMPRINT",EDGE,{"derivedFrom":subQ2}),1.0]])]});}
            var Q21;
            {var subQ1=sQuery(id+"F0.wireOp",EDGE,"E27.2.19.0");Q21=makeQuery(id+"F0.imprint","IMPRINT",FACE,{"disambiguationData":[TD([[makeQuery(id+"F0.imprint","IMPRINT",EDGE,{"derivedFrom":subQ1}),1.0]])]});}
            var Q22;
            {var subQ1=sQuery(id+"F0.wireOp",EDGE,"E27.2.20.0");Q22=makeQuery(id+"F0.imprint","IMPRINT",FACE,{"disambiguationData":[TD([[makeQuery(id+"F0.imprint","IMPRINT",EDGE,{"derivedFrom":subQ1}),1.0]])]});}
            var Q23;
            {var subQ2=sQuery(id+"F0.wireOp",EDGE,"E27.2.23.0");Q23=makeQuery(id+"F0.imprint","IMPRINT",FACE,{"disambiguationData":[TD([[makeQuery(id+"F0.imprint","IMPRINT",EDGE,{"derivedFrom":subQ2}),1.0]])]});}
            var Q24;
            {var subQ1=sQuery(id+"F0.wireOp",EDGE,"E27.2.28.0");Q24=makeQuery(id+"F0.imprint","IMPRINT",FACE,{"disambiguationData":[TD([[makeQuery(id+"F0.imprint","IMPRINT",EDGE,{"derivedFrom":subQ1}),1.0]])]});}
            var Q25;
            {var subQ2=sQuery(id+"F0.wireOp",EDGE,"E27.2.29.0");Q25=makeQuery(id+"F0.imprint","IMPRINT",FACE,{"disambiguationData":[TD([[makeQuery(id+"F0.imprint","IMPRINT",EDGE,{"derivedFrom":subQ2}),1.0]])]});}
            var Q26;
            {var subQ1=sQuery(id+"F0.wireOp",EDGE,"E27.2.31.0");Q26=makeQuery(id+"F0.imprint","IMPRINT",FACE,{"disambiguationData":[TD([[makeQuery(id+"F0.imprint","IMPRINT",EDGE,{"derivedFrom":subQ1}),1.0]])]});}
            var Q27;
            {var subQ1=sQuery(id+"F0.wireOp",EDGE,"E27.2.32.0");Q27=makeQuery(id+"F0.imprint","IMPRINT",FACE,{"disambiguationData":[TD([[makeQuery(id+"F0.imprint","IMPRINT",EDGE,{"derivedFrom":subQ1}),1.0]])]});}
            var Q28;
            {var subQ1=sQuery(id+"F0.wireOp",EDGE,"E27.2.33.0");Q28=makeQuery(id+"F0.imprint","IMPRINT",FACE,{"disambiguationData":[TD([[makeQuery(id+"F0.imprint","IMPRINT",EDGE,{"derivedFrom":subQ1}),1.0]])]});}
            var Q29;
            {var subQ1=sQuery(id+"F0.wireOp",EDGE,"E27.2.22.0");Q29=makeQuery(id+"F0.imprint","IMPRINT",FACE,{"disambiguationData":[TD([[makeQuery(id+"F0.imprint","IMPRINT",EDGE,{"derivedFrom":subQ1}),1.0]])]});}
            var Q30;
            {var subQ2=sQuery(id+"F0.wireOp",EDGE,"E27.2.24.0");Q30=makeQuery(id+"F0.imprint","IMPRINT",FACE,{"disambiguationData":[TD([[makeQuery(id+"F0.imprint","IMPRINT",EDGE,{"derivedFrom":subQ2}),1.0]])]});}
            var Q31;
            {var subQ1=sQuery(id+"F0.wireOp",EDGE,"E27.2.25.0");Q31=makeQuery(id+"F0.imprint","IMPRINT",FACE,{"disambiguationData":[TD([[makeQuery(id+"F0.imprint","IMPRINT",EDGE,{"derivedFrom":subQ1}),1.0]])]});}
            var Q32;
            {var subQ1=sQuery(id+"F0.wireOp",EDGE,"E27.2.26.0");Q32=makeQuery(id+"F0.imprint","IMPRINT",FACE,{"disambiguationData":[TD([[makeQuery(id+"F0.imprint","IMPRINT",EDGE,{"derivedFrom":subQ1}),1.0]])]});}
            var Q33;
            {var subQ1=sQuery(id+"F0.wireOp",EDGE,"E27.2.27.0");Q33=makeQuery(id+"F0.imprint","IMPRINT",FACE,{"disambiguationData":[TD([[makeQuery(id+"F0.imprint","IMPRINT",EDGE,{"derivedFrom":subQ1}),1.0]])]});}
            var Q34;
            {var subQ1=sQuery(id+"F0.wireOp",EDGE,"E27.2.30.0");Q34=makeQuery(id+"F0.imprint","IMPRINT",FACE,{"disambiguationData":[TD([[makeQuery(id+"F0.imprint","IMPRINT",EDGE,{"derivedFrom":subQ1}),1.0]])]});}
            var Q35;
            {var subQ2=sQuery(id+"F0.wireOp",EDGE,"E27.2.34.0");Q35=makeQuery(id+"F0.imprint","IMPRINT",FACE,{"disambiguationData":[TD([[makeQuery(id+"F0.imprint","IMPRINT",EDGE,{"derivedFrom":subQ2}),1.0]])]});}
            var Q36;
            {var subQ1=sQuery(id+"F0.wireOp",EDGE,"E27.2.36.0");Q36=makeQuery(id+"F0.imprint","IMPRINT",FACE,{"disambiguationData":[TD([[makeQuery(id+"F0.imprint","IMPRINT",EDGE,{"derivedFrom":subQ1}),1.0]])]});}
            var Q37;
            {var subQ2=sQuery(id+"F0.wireOp",EDGE,"E27.2.35.0");Q37=makeQuery(id+"F0.imprint","IMPRINT",FACE,{"disambiguationData":[TD([[makeQuery(id+"F0.imprint","IMPRINT",EDGE,{"derivedFrom":subQ2}),1.0]])]});}
            var Q38;
            {var subQ1=sQuery(id+"F0.wireOp",EDGE,"E27.2.37.0");Q38=makeQuery(id+"F0.imprint","IMPRINT",FACE,{"disambiguationData":[TD([[makeQuery(id+"F0.imprint","IMPRINT",EDGE,{"derivedFrom":subQ1}),1.0]])]});}
            var Q39;
            {var subQ1=sQuery(id+"F0.wireOp",EDGE,"E27.2.38.0");Q39=makeQuery(id+"F0.imprint","IMPRINT",FACE,{"disambiguationData":[TD([[makeQuery(id+"F0.imprint","IMPRINT",EDGE,{"derivedFrom":subQ1}),1.0]])]});}
            var Q40;
            {var subQ1=sQuery(id+"F0.wireOp",EDGE,"E27.2.39.0");Q40=makeQuery(id+"F0.imprint","IMPRINT",FACE,{"disambiguationData":[TD([[makeQuery(id+"F0.imprint","IMPRINT",EDGE,{"derivedFrom":subQ1}),1.0]])]});}
            var Q41;
            {var subQ2=sQuery(id+"F0.wireOp",EDGE,"E27.2.40.0");Q41=makeQuery(id+"F0.imprint","IMPRINT",FACE,{"disambiguationData":[TD([[makeQuery(id+"F0.imprint","IMPRINT",EDGE,{"derivedFrom":subQ2}),1.0]])]});}
            var Q42;
            {var subQ1=sQuery(id+"F0.wireOp",EDGE,"E27.2.41.0");Q42=makeQuery(id+"F0.imprint","IMPRINT",FACE,{"disambiguationData":[TD([[makeQuery(id+"F0.imprint","IMPRINT",EDGE,{"derivedFrom":subQ1}),1.0]])]});}
            var Q43;
            {var subQ1=sQuery(id+"F0.wireOp",EDGE,"E27.2.42.0");Q43=makeQuery(id+"F0.imprint","IMPRINT",FACE,{"disambiguationData":[TD([[makeQuery(id+"F0.imprint","IMPRINT",EDGE,{"derivedFrom":subQ1}),1.0]])]});}
            var Q44;
            {var subQ1=sQuery(id+"F0.wireOp",EDGE,"E27.2.44.0");Q44=makeQuery(id+"F0.imprint","IMPRINT",FACE,{"disambiguationData":[TD([[makeQuery(id+"F0.imprint","IMPRINT",EDGE,{"derivedFrom":subQ1}),1.0]])]});}
            var Q45;
            {var subQ2=sQuery(id+"F0.wireOp",EDGE,"E27.2.45.0");Q45=makeQuery(id+"F0.imprint","IMPRINT",FACE,{"disambiguationData":[TD([[makeQuery(id+"F0.imprint","IMPRINT",EDGE,{"derivedFrom":subQ2}),1.0]])]});}
            var Q46;
            {var subQ2=sQuery(id+"F0.wireOp",EDGE,"E27.2.46.0");Q46=makeQuery(id+"F0.imprint","IMPRINT",FACE,{"disambiguationData":[TD([[makeQuery(id+"F0.imprint","IMPRINT",EDGE,{"derivedFrom":subQ2}),1.0]])]});}
            var Q47;
            {var subQ1=sQuery(id+"F0.wireOp",EDGE,"E27.2.47.0");Q47=makeQuery(id+"F0.imprint","IMPRINT",FACE,{"disambiguationData":[TD([[makeQuery(id+"F0.imprint","IMPRINT",EDGE,{"derivedFrom":subQ1}),1.0]])]});}
            var Q48;
            {var subQ1=sQuery(id+"F0.wireOp",EDGE,"E27.2.43.0");Q48=makeQuery(id+"F0.imprint","IMPRINT",FACE,{"disambiguationData":[TD([[makeQuery(id+"F0.imprint","IMPRINT",EDGE,{"derivedFrom":subQ1}),1.0]])]});}
            var Q49;
            {var subQ1=sQuery(id+"F0.wireOp",EDGE,"E27.2.48.0");Q49=makeQuery(id+"F0.imprint","IMPRINT",FACE,{"disambiguationData":[TD([[makeQuery(id+"F0.imprint","IMPRINT",EDGE,{"derivedFrom":subQ1}),1.0]])]});}
            var Q50;
            {var subQ1=sQuery(id+"F0.wireOp",EDGE,"E27.2.49.0");Q50=makeQuery(id+"F0.imprint","IMPRINT",FACE,{"disambiguationData":[TD([[makeQuery(id+"F0.imprint","IMPRINT",EDGE,{"derivedFrom":subQ1}),1.0]])]});}
            var Q51;
            {var subQ1=sQuery(id+"F0.wireOp",EDGE,"E27.2.50.0");Q51=makeQuery(id+"F0.imprint","IMPRINT",FACE,{"disambiguationData":[TD([[makeQuery(id+"F0.imprint","IMPRINT",EDGE,{"derivedFrom":subQ1}),1.0]])]});}
            var Q52;
            {var subQ2=sQuery(id+"F0.wireOp",EDGE,"E27.2.51.0");Q52=makeQuery(id+"F0.imprint","IMPRINT",FACE,{"disambiguationData":[TD([[makeQuery(id+"F0.imprint","IMPRINT",EDGE,{"derivedFrom":subQ2}),1.0]])]});}
            var Q53;
            {var subQ1=sQuery(id+"F0.wireOp",EDGE,"E27.2.52.0");Q53=makeQuery(id+"F0.imprint","IMPRINT",FACE,{"disambiguationData":[TD([[makeQuery(id+"F0.imprint","IMPRINT",EDGE,{"derivedFrom":subQ1}),1.0]])]});}
            var Q54;
            {var subQ1=sQuery(id+"F0.wireOp",EDGE,"E27.2.53.0");Q54=makeQuery(id+"F0.imprint","IMPRINT",FACE,{"disambiguationData":[TD([[makeQuery(id+"F0.imprint","IMPRINT",EDGE,{"derivedFrom":subQ1}),1.0]])]});}
            var Q55;
            {var subQ1=sQuery(id+"F0.wireOp",EDGE,"E27.2.54.0");Q55=makeQuery(id+"F0.imprint","IMPRINT",FACE,{"disambiguationData":[TD([[makeQuery(id+"F0.imprint","IMPRINT",EDGE,{"derivedFrom":subQ1}),1.0]])]});}
            var Q56;
            {var subQ1=sQuery(id+"F0.wireOp",EDGE,"E27.2.55.0");Q56=makeQuery(id+"F0.imprint","IMPRINT",FACE,{"disambiguationData":[TD([[makeQuery(id+"F0.imprint","IMPRINT",EDGE,{"derivedFrom":subQ1}),1.0]])]});}
            var Q57;
            {var subQ2=sQuery(id+"F0.wireOp",EDGE,"E27.2.56.0");Q57=makeQuery(id+"F0.imprint","IMPRINT",FACE,{"disambiguationData":[TD([[makeQuery(id+"F0.imprint","IMPRINT",EDGE,{"derivedFrom":subQ2}),1.0]])]});}
            var Q58;
            {var subQ2=sQuery(id+"F0.wireOp",EDGE,"E27.2.57.0");Q58=makeQuery(id+"F0.imprint","IMPRINT",FACE,{"disambiguationData":[TD([[makeQuery(id+"F0.imprint","IMPRINT",EDGE,{"derivedFrom":subQ2}),1.0]])]});}
            var Q59;
            {var subQ1=sQuery(id+"F0.wireOp",EDGE,"E27.2.60.0");Q59=makeQuery(id+"F0.imprint","IMPRINT",FACE,{"disambiguationData":[TD([[makeQuery(id+"F0.imprint","IMPRINT",EDGE,{"derivedFrom":subQ1}),1.0]])]});}
            var Q60;
            {var subQ1=sQuery(id+"F0.wireOp",EDGE,"E27.2.59.0");Q60=makeQuery(id+"F0.imprint","IMPRINT",FACE,{"disambiguationData":[TD([[makeQuery(id+"F0.imprint","IMPRINT",EDGE,{"derivedFrom":subQ1}),1.0]])]});}
            var Q61;
            {var subQ1=sQuery(id+"F0.wireOp",EDGE,"E27.2.58.0");Q61=makeQuery(id+"F0.imprint","IMPRINT",FACE,{"disambiguationData":[TD([[makeQuery(id+"F0.imprint","IMPRINT",EDGE,{"derivedFrom":subQ1}),1.0]])]});}
            var Q62;
            {var subQ1=sQuery(id+"F0.wireOp",EDGE,"E27.2.61.0");Q62=makeQuery(id+"F0.imprint","IMPRINT",FACE,{"disambiguationData":[TD([[makeQuery(id+"F0.imprint","IMPRINT",EDGE,{"derivedFrom":subQ1}),1.0]])]});}
            var Q63;
            {var subQ2=sQuery(id+"F0.wireOp",EDGE,"E27.2.62.0");Q63=makeQuery(id+"F0.imprint","IMPRINT",FACE,{"disambiguationData":[TD([[makeQuery(id+"F0.imprint","IMPRINT",EDGE,{"derivedFrom":subQ2}),1.0]])]});}
            var Q64;
            {var subQ1=sQuery(id+"F0.wireOp",EDGE,"E27.2.63.0");Q64=makeQuery(id+"F0.imprint","IMPRINT",FACE,{"disambiguationData":[TD([[makeQuery(id+"F0.imprint","IMPRINT",EDGE,{"derivedFrom":subQ1}),1.0]])]});}
            var Q65;
            {var subQ1=sQuery(id+"F0.wireOp",EDGE,"E27.2.64.0");Q65=makeQuery(id+"F0.imprint","IMPRINT",FACE,{"disambiguationData":[TD([[makeQuery(id+"F0.imprint","IMPRINT",EDGE,{"derivedFrom":subQ1}),1.0]])]});}
            var Q66;
            {var subQ1=sQuery(id+"F0.wireOp",EDGE,"E27.2.66.0");Q66=makeQuery(id+"F0.imprint","IMPRINT",FACE,{"disambiguationData":[TD([[makeQuery(id+"F0.imprint","IMPRINT",EDGE,{"derivedFrom":subQ1}),1.0]])]});}
            var Q67;
            {var subQ2=sQuery(id+"F0.wireOp",EDGE,"E27.2.68.0");Q67=makeQuery(id+"F0.imprint","IMPRINT",FACE,{"disambiguationData":[TD([[makeQuery(id+"F0.imprint","IMPRINT",EDGE,{"derivedFrom":subQ2}),1.0]])]});}
            var Q68;
            {var subQ1=sQuery(id+"F0.wireOp",EDGE,"E27.2.69.0");Q68=makeQuery(id+"F0.imprint","IMPRINT",FACE,{"disambiguationData":[TD([[makeQuery(id+"F0.imprint","IMPRINT",EDGE,{"derivedFrom":subQ1}),1.0]])]});}
            var Q69;
            {var subQ1=sQuery(id+"F0.wireOp",EDGE,"E27.2.70.0");Q69=makeQuery(id+"F0.imprint","IMPRINT",FACE,{"disambiguationData":[TD([[makeQuery(id+"F0.imprint","IMPRINT",EDGE,{"derivedFrom":subQ1}),1.0]])]});}
            var Q70;
            {var subQ1=sQuery(id+"F0.wireOp",EDGE,"E27.2.71.0");Q70=makeQuery(id+"F0.imprint","IMPRINT",FACE,{"disambiguationData":[TD([[makeQuery(id+"F0.imprint","IMPRINT",EDGE,{"derivedFrom":subQ1}),1.0]])]});}
            var Q71;
            {var subQ1=sQuery(id+"F0.wireOp",EDGE,"E27.2.72.0");Q71=makeQuery(id+"F0.imprint","IMPRINT",FACE,{"disambiguationData":[TD([[makeQuery(id+"F0.imprint","IMPRINT",EDGE,{"derivedFrom":subQ1}),1.0]])]});}
            var Q72;
            {var subQ2=sQuery(id+"F0.wireOp",EDGE,"E27.2.73.0");Q72=makeQuery(id+"F0.imprint","IMPRINT",FACE,{"disambiguationData":[TD([[makeQuery(id+"F0.imprint","IMPRINT",EDGE,{"derivedFrom":subQ2}),1.0]])]});}
            var Q73;
            {var subQ1=sQuery(id+"F0.wireOp",EDGE,"E27.2.74.0");Q73=makeQuery(id+"F0.imprint","IMPRINT",FACE,{"disambiguationData":[TD([[makeQuery(id+"F0.imprint","IMPRINT",EDGE,{"derivedFrom":subQ1}),1.0]])]});}
            var Q74;
            {var subQ1=sQuery(id+"F0.wireOp",EDGE,"E27.2.75.0");Q74=makeQuery(id+"F0.imprint","IMPRINT",FACE,{"disambiguationData":[TD([[makeQuery(id+"F0.imprint","IMPRINT",EDGE,{"derivedFrom":subQ1}),1.0]])]});}
            var Q75;
            {var subQ2=sQuery(id+"F0.wireOp",EDGE,"E27.2.67.0");Q75=makeQuery(id+"F0.imprint","IMPRINT",FACE,{"disambiguationData":[TD([[makeQuery(id+"F0.imprint","IMPRINT",EDGE,{"derivedFrom":subQ2}),1.0]])]});}
            var Q76;
            {var subQ1=sQuery(id+"F0.wireOp",EDGE,"E27.2.65.0");Q76=makeQuery(id+"F0.imprint","IMPRINT",FACE,{"disambiguationData":[TD([[makeQuery(id+"F0.imprint","IMPRINT",EDGE,{"derivedFrom":subQ1}),1.0]])]});}
            var Q77;
            {var subQ1=sQuery(id+"F0.wireOp",EDGE,"E27.2.76.0");Q77=makeQuery(id+"F0.imprint","IMPRINT",FACE,{"disambiguationData":[TD([[makeQuery(id+"F0.imprint","IMPRINT",EDGE,{"derivedFrom":subQ1}),1.0]])]});}
            var Q78;
            {var subQ1=sQuery(id+"F0.wireOp",EDGE,"E27.2.77.0");Q78=makeQuery(id+"F0.imprint","IMPRINT",FACE,{"disambiguationData":[TD([[makeQuery(id+"F0.imprint","IMPRINT",EDGE,{"derivedFrom":subQ1}),1.0]])]});}
            var Q79;
            {var subQ2=sQuery(id+"F0.wireOp",EDGE,"E27.2.78.0");Q79=makeQuery(id+"F0.imprint","IMPRINT",FACE,{"disambiguationData":[TD([[makeQuery(id+"F0.imprint","IMPRINT",EDGE,{"derivedFrom":subQ2}),1.0]])]});}
            var Q80;
            {var subQ1=sQuery(id+"F0.wireOp",EDGE,"E27.2.79.0");Q80=makeQuery(id+"F0.imprint","IMPRINT",FACE,{"disambiguationData":[TD([[makeQuery(id+"F0.imprint","IMPRINT",EDGE,{"derivedFrom":subQ1}),1.0]])]});}
            var Q81;
            {var subQ1=sQuery(id+"F0.wireOp",EDGE,"E27.2.80.0");Q81=makeQuery(id+"F0.imprint","IMPRINT",FACE,{"disambiguationData":[TD([[makeQuery(id+"F0.imprint","IMPRINT",EDGE,{"derivedFrom":subQ1}),1.0]])]});}
            var Q82;
            {var subQ1=sQuery(id+"F0.wireOp",EDGE,"E27.2.81.0");Q82=makeQuery(id+"F0.imprint","IMPRINT",FACE,{"disambiguationData":[TD([[makeQuery(id+"F0.imprint","IMPRINT",EDGE,{"derivedFrom":subQ1}),1.0]])]});}
            var Q83;
            {var subQ2=sQuery(id+"F0.wireOp",EDGE,"E27.2.82.0");Q83=makeQuery(id+"F0.imprint","IMPRINT",FACE,{"disambiguationData":[TD([[makeQuery(id+"F0.imprint","IMPRINT",EDGE,{"derivedFrom":subQ2}),1.0]])]});}
            var Q84;
            {var subQ2=sQuery(id+"F0.wireOp",EDGE,"E27.2.83.0");Q84=makeQuery(id+"F0.imprint","IMPRINT",FACE,{"disambiguationData":[TD([[makeQuery(id+"F0.imprint","IMPRINT",EDGE,{"derivedFrom":subQ2}),1.0]])]});}
            var Q85;
            {var subQ1=sQuery(id+"F0.wireOp",EDGE,"E27.2.84.0");Q85=makeQuery(id+"F0.imprint","IMPRINT",FACE,{"disambiguationData":[TD([[makeQuery(id+"F0.imprint","IMPRINT",EDGE,{"derivedFrom":subQ1}),1.0]])]});}
            var Q86;
            {var subQ1=sQuery(id+"F0.wireOp",EDGE,"E27.2.86.0");Q86=makeQuery(id+"F0.imprint","IMPRINT",FACE,{"disambiguationData":[TD([[makeQuery(id+"F0.imprint","IMPRINT",EDGE,{"derivedFrom":subQ1}),1.0]])]});}
            var Q87;
            {var subQ1=sQuery(id+"F0.wireOp",EDGE,"E27.2.87.0");Q87=makeQuery(id+"F0.imprint","IMPRINT",FACE,{"disambiguationData":[TD([[makeQuery(id+"F0.imprint","IMPRINT",EDGE,{"derivedFrom":subQ1}),1.0]])]});}
            var Q88;
            {var subQ2=sQuery(id+"F0.wireOp",EDGE,"E27.2.88.0");Q88=makeQuery(id+"F0.imprint","IMPRINT",FACE,{"disambiguationData":[TD([[makeQuery(id+"F0.imprint","IMPRINT",EDGE,{"derivedFrom":subQ2}),1.0]])]});}
            var Q89;
            {var subQ1=sQuery(id+"F0.wireOp",EDGE,"E27.2.89.0");Q89=makeQuery(id+"F0.imprint","IMPRINT",FACE,{"disambiguationData":[TD([[makeQuery(id+"F0.imprint","IMPRINT",EDGE,{"derivedFrom":subQ1}),1.0]])]});}
            var Q90;
            {var subQ1=sQuery(id+"F0.wireOp",EDGE,"E27.2.85.0");Q90=makeQuery(id+"F0.imprint","IMPRINT",FACE,{"disambiguationData":[TD([[makeQuery(id+"F0.imprint","IMPRINT",EDGE,{"derivedFrom":subQ1}),1.0]])]});}
            var Q91;
            {var subQ1=sQuery(id+"F0.wireOp",EDGE,"E27.2.90.0");Q91=makeQuery(id+"F0.imprint","IMPRINT",FACE,{"disambiguationData":[TD([[makeQuery(id+"F0.imprint","IMPRINT",EDGE,{"derivedFrom":subQ1}),1.0]])]});}
            var Q92;
            {var subQ1=sQuery(id+"F0.wireOp",EDGE,"E27.2.91.0");Q92=makeQuery(id+"F0.imprint","IMPRINT",FACE,{"disambiguationData":[TD([[makeQuery(id+"F0.imprint","IMPRINT",EDGE,{"derivedFrom":subQ1}),1.0]])]});}
            var Q93;
            {var subQ1=sQuery(id+"F0.wireOp",EDGE,"E27.2.92.0");Q93=makeQuery(id+"F0.imprint","IMPRINT",FACE,{"disambiguationData":[TD([[makeQuery(id+"F0.imprint","IMPRINT",EDGE,{"derivedFrom":subQ1}),1.0]])]});}
            var Q94;
            {var subQ2=sQuery(id+"F0.wireOp",EDGE,"E27.2.93.0");Q94=makeQuery(id+"F0.imprint","IMPRINT",FACE,{"disambiguationData":[TD([[makeQuery(id+"F0.imprint","IMPRINT",EDGE,{"derivedFrom":subQ2}),1.0]])]});}
            var Q95;
            {var subQ2=sQuery(id+"F0.wireOp",EDGE,"E27.2.94.0");Q95=makeQuery(id+"F0.imprint","IMPRINT",FACE,{"disambiguationData":[TD([[makeQuery(id+"F0.imprint","IMPRINT",EDGE,{"derivedFrom":subQ2}),1.0]])]});}
            var Q96;
            {var subQ1=sQuery(id+"F0.wireOp",EDGE,"E27.2.95.0");Q96=makeQuery(id+"F0.imprint","IMPRINT",FACE,{"disambiguationData":[TD([[makeQuery(id+"F0.imprint","IMPRINT",EDGE,{"derivedFrom":subQ1}),1.0]])]});}
            var Q97;
            {var subQ1=sQuery(id+"F0.wireOp",EDGE,"E27.2.96.0");Q97=makeQuery(id+"F0.imprint","IMPRINT",FACE,{"disambiguationData":[TD([[makeQuery(id+"F0.imprint","IMPRINT",EDGE,{"derivedFrom":subQ1}),1.0]])]});}
            var Q98;
            {var subQ1=sQuery(id+"F0.wireOp",EDGE,"E27.2.97.0");Q98=makeQuery(id+"F0.imprint","IMPRINT",FACE,{"disambiguationData":[TD([[makeQuery(id+"F0.imprint","IMPRINT",EDGE,{"derivedFrom":subQ1}),1.0]])]});}
            var Q99;
            {var subQ1=sQuery(id+"F0.wireOp",EDGE,"E27.2.98.0");Q99=makeQuery(id+"F0.imprint","IMPRINT",FACE,{"disambiguationData":[TD([[makeQuery(id+"F0.imprint","IMPRINT",EDGE,{"derivedFrom":subQ1}),1.0]])]});}
            var Q100;
            {var subQ2=sQuery(id+"F0.wireOp",EDGE,"E27.2.99.0");Q100=makeQuery(id+"F0.imprint","IMPRINT",FACE,{"disambiguationData":[TD([[makeQuery(id+"F0.imprint","IMPRINT",EDGE,{"derivedFrom":subQ2}),1.0]])]});}
            var Q101;
            {var subQ1=sQuery(id+"F0.wireOp",EDGE,"E27.2.100.0");Q101=makeQuery(id+"F0.imprint","IMPRINT",FACE,{"disambiguationData":[TD([[makeQuery(id+"F0.imprint","IMPRINT",EDGE,{"derivedFrom":subQ1}),1.0]])]});}
            var Q102;
            {var subQ2=sQuery(id+"F0.wireOp",EDGE,"E27.2.105.0");Q102=makeQuery(id+"F0.imprint","IMPRINT",FACE,{"disambiguationData":[TD([[makeQuery(id+"F0.imprint","IMPRINT",EDGE,{"derivedFrom":subQ2}),1.0]])]});}
            var Q103;
            {var subQ2=sQuery(id+"F0.wireOp",EDGE,"E27.2.104.0");Q103=makeQuery(id+"F0.imprint","IMPRINT",FACE,{"disambiguationData":[TD([[makeQuery(id+"F0.imprint","IMPRINT",EDGE,{"derivedFrom":subQ2}),1.0]])]});}
            var Q104;
            {var subQ1=sQuery(id+"F0.wireOp",EDGE,"E27.2.101.0");Q104=makeQuery(id+"F0.imprint","IMPRINT",FACE,{"disambiguationData":[TD([[makeQuery(id+"F0.imprint","IMPRINT",EDGE,{"derivedFrom":subQ1}),1.0]])]});}
            var Q105;
            {var subQ1=sQuery(id+"F0.wireOp",EDGE,"E27.2.102.0");Q105=makeQuery(id+"F0.imprint","IMPRINT",FACE,{"disambiguationData":[TD([[makeQuery(id+"F0.imprint","IMPRINT",EDGE,{"derivedFrom":subQ1}),1.0]])]});}
            var Q106;
            {var subQ1=sQuery(id+"F0.wireOp",EDGE,"E27.2.103.0");Q106=makeQuery(id+"F0.imprint","IMPRINT",FACE,{"disambiguationData":[TD([[makeQuery(id+"F0.imprint","IMPRINT",EDGE,{"derivedFrom":subQ1}),1.0]])]});}
            extrude(context, id + "F2", {"entities" : qUnion([Q0, Q1, Q2, Q3, Q4, Q5, Q6, Q7, Q8, Q9, Q10, Q11, Q12, Q13, Q14, Q15, Q16, Q17, Q18, Q19, Q20, Q21, Q22, Q23, Q24, Q25, Q26, Q27, Q28, Q29, Q30, Q31, Q32, Q33, Q34, Q35, Q36, Q37, Q38, Q39, Q40, Q41, Q42, Q43, Q44, Q45, Q46, Q47, Q48, Q49, Q50, Q51, Q52, Q53, Q54, Q55, Q56, Q57, Q58, Q59, Q60, Q61, Q62, Q63, Q64, Q65, Q66, Q67, Q68, Q69, Q70, Q71, Q72, Q73, Q74, Q75, Q76, Q77, Q78, Q79, Q80, Q81, Q82, Q83, Q84, Q85, Q86, Q87, Q88, Q89, Q90, Q91, Q92, Q93, Q94, Q95, Q96, Q97, Q98, Q99, Q100, Q101, Q102, Q103, Q104, Q105, Q106]), "depth" : 12 * mm, "offsetDistance" : 25 * mm});
        }
        {
            var Q0;
            Q0=sQuery(id+"F0.wireOp",VERTEX,"E20.MirrorC.center");
            var Q1;
            Q1=sQuery(id+"F0.wireOp",VERTEX,"E11.center");
            var Q2;
            Q2=sQuery(id+"F0.wireOp",VERTEX,"E13.center");
            var Q3;
            Q3=sQuery(id+"F0.wireOp",VERTEX,"E18.center");
            var Q4;
            Q4=sQuery(id+"F0.wireOp",VERTEX,"E16.MirrorC.center");
            var Q5;
            Q5=sQuery(id+"F0.wireOp",VERTEX,"E12.center");
            var Q6;
            Q6=makeQuery(id+"F1.opExtrude","SWEPT_BODY",BODY,{"disambiguationData":[OSD([sQuery(id+"F0.wireOp",EDGE,"E4"),sQuery(id+"F0.wireOp",EDGE,"E6")])]});
            hole(context, id + "F3", {"style" : HoleStyle.SIMPLE, "endStyle" : HoleEndStyle.BLIND, "oppositeDirection" : true, "holeDiameter" : 2.5 * mm, "holeDepth" : 4 * mm, "isTappedThrough" : true, "tappedDepth" : 12 * mm, "tapClearance" : 3, "locations" : qUnion([Q0, Q1, Q2, Q3, Q4, Q5]), "scope" : qUnion([Q6])});
        }
        {
            var Q0;
            Q0=sQuery(id+"F0.wireOp",VERTEX,"E21.center");
            var Q1;
            Q1=sQuery(id+"F0.wireOp",VERTEX,"E22.center");
            var Q2;
            Q2=makeQuery(id+"F1.opExtrude","SWEPT_BODY",BODY,{"disambiguationData":[OSD([sQuery(id+"F0.wireOp",EDGE,"E4"),sQuery(id+"F0.wireOp",EDGE,"E6")])]});
            hole(context, id + "F4", {"style" : HoleStyle.SIMPLE, "endStyle" : HoleEndStyle.BLIND, "oppositeDirection" : true, "holeDiameter" : 3.5 * mm, "holeDepth" : 4 * mm, "isTappedThrough" : true, "tappedDepth" : 12 * mm, "tapClearance" : 3, "locations" : qUnion([Q0, Q1]), "scope" : qUnion([Q2])});
        }
    });
